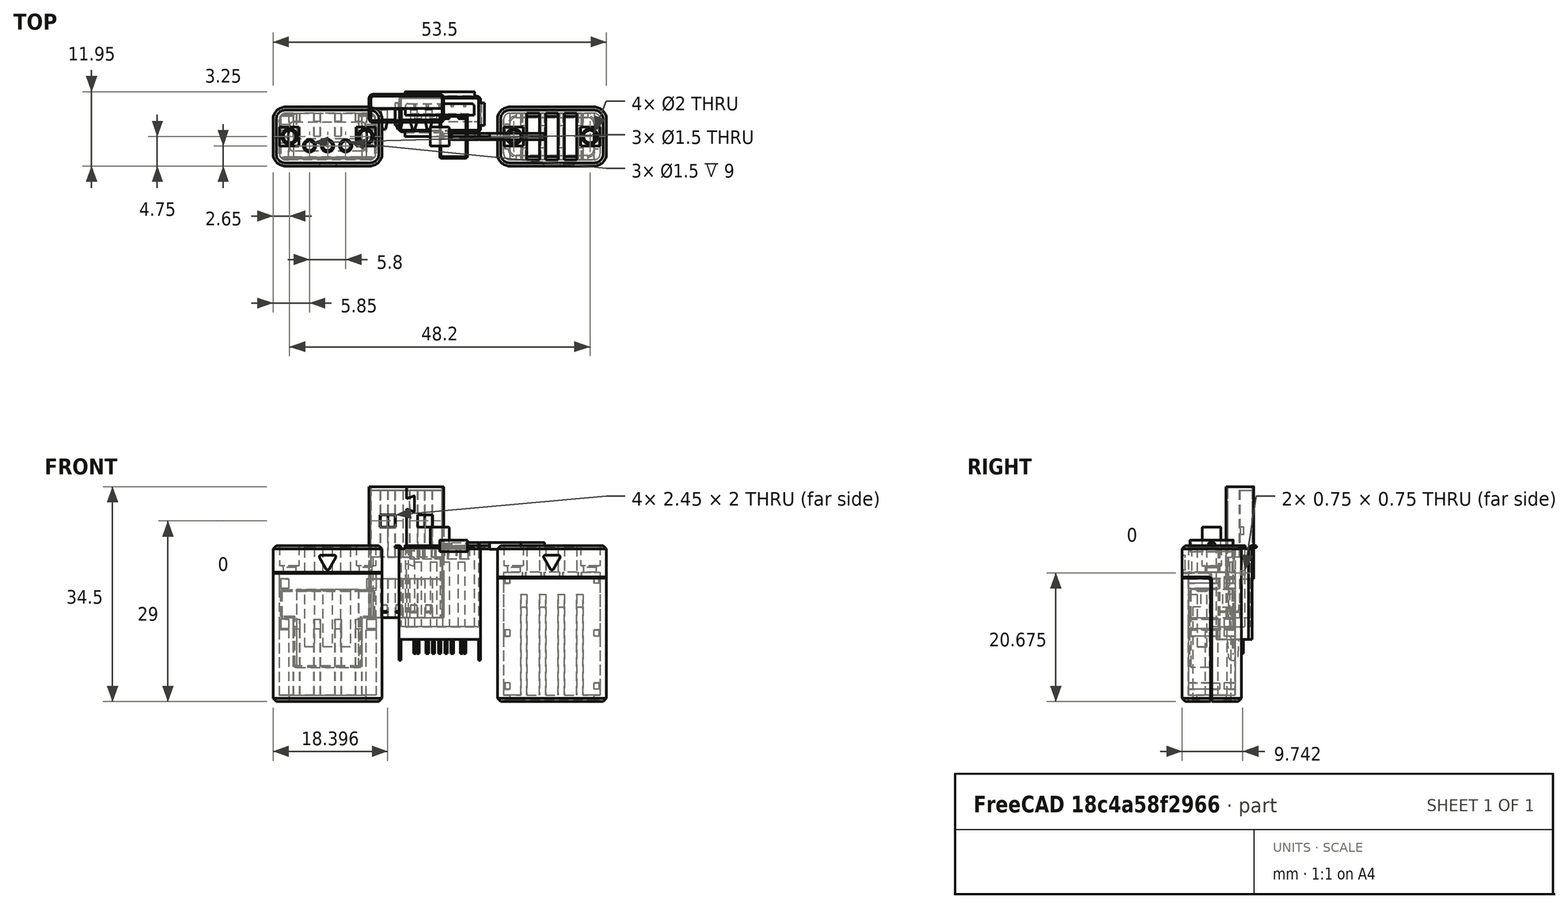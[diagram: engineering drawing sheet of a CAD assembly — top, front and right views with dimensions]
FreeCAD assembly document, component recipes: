
FREECAD ASSEMBLY — COMPONENT RECIPES ("test_v0.1_with_parts_I_have")

This assembly document has 13 components, labeled P0..P12 below (a component is one placed body or linked part). 10 of them carry a construction recipe — the FreeCAD feature program that regenerates the part from scratch, quoted from this document or its linked companion documents; the rest are supplied as boundary geometry only. No exploded tour is included for this assembly.
COMPONENT P0 — recipe-attached ("Housing-USB_Female", modeled in this document).
Construction recipe (the document's own serialized feature program — sketch geometry with constraints, then the solid features built on it; lengths are millimeters unless a unit is written):

FEATURE [PartDesign::FeatureBase] Clone
  BaseFeature = -> Chamfer002
FEATURE [Sketcher::SketchObject] Sketch020
  FullyConstrained = true
  MapMode = 5
  Support = -> [XY_Plane009]
  sketch-geometry (16):
    g0: LineSegment StartX=-1 StartY=3.75 StartZ=0 EndX=1 EndY=3.75 EndZ=0
    g1: LineSegment StartX=1 StartY=3.75 StartZ=0 EndX=1 EndY=3.25 EndZ=0
    g2: LineSegment StartX=1 StartY=3.25 StartZ=0 EndX=-1 EndY=3.25 EndZ=0
    g3: LineSegment StartX=-1 StartY=3.25 StartZ=0 EndX=-1 EndY=3.75 EndZ=0
    g4: LineSegment StartX=2 StartY=3.75 StartZ=0 EndX=4 EndY=3.75 EndZ=0
    g5: LineSegment StartX=4 StartY=3.75 StartZ=0 EndX=4 EndY=3.25 EndZ=0
    g6: LineSegment StartX=4 StartY=3.25 StartZ=0 EndX=2 EndY=3.25 EndZ=0
    g7: LineSegment StartX=2 StartY=3.25 StartZ=0 EndX=2 EndY=3.75 EndZ=0
    g8: LineSegment StartX=-4 StartY=3.75 StartZ=0 EndX=-2 EndY=3.75 EndZ=0
    g9: LineSegment StartX=-2 StartY=3.75 StartZ=0 EndX=-2 EndY=3.25 EndZ=0
    g10: LineSegment StartX=-2 StartY=3.25 StartZ=0 EndX=-4 EndY=3.25 EndZ=0
    g11: LineSegment StartX=-4 StartY=3.25 StartZ=0 EndX=-4 EndY=3.75 EndZ=0
    g12: LineSegment StartX=-2 StartY=3.75 StartZ=0 EndX=-1 EndY=3.75 EndZ=0
    g13: LineSegment StartX=1 StartY=3.75 StartZ=0 EndX=2 EndY=3.75 EndZ=0
    g14: LineSegment StartX=0 StartY=3.75 StartZ=0 EndX=0 EndY=3.5 EndZ=0
    g15: LineSegment StartX=0 StartY=3.5 StartZ=0 EndX=0 EndY=3.25 EndZ=0
  constraints (46):
    c: Coincident(g0,g1)
    c: Coincident(g1,g2)
    c: Coincident(g2,g3)
    c: Coincident(g3,g0)
    c: Horizontal(g2)
    c: Vertical(g1)
    c: Vertical(g3)
    c: Coincident(g4,g5)
    c: Coincident(g5,g6)
    c: Coincident(g6,g7)
    c: Coincident(g7,g4)
    c: Horizontal(g4)
    c: Horizontal(g6)
    c: Vertical(g5)
    c: Vertical(g7)
    c: Coincident(g8,g9)
    c: Coincident(g9,g10)
    c: Coincident(g10,g11)
    c: Coincident(g11,g8)
    c: Horizontal(g8)
    c: Horizontal(g10)
    c: Vertical(g9)
    c: Vertical(g11)
    c: Equal(g0,g8)
    c: Equal(g8,g4)
    c: Equal(g3,g7)
    c: Equal(g7,g11)
    c: Coincident(g12,g8)
    c: Coincident(g12,g0)
    c: Horizontal(g12)
    c: Coincident(g13,g0)
    c: Coincident(g13,g4)
    c: Horizontal(g13)
    c: PointOnObject(g14,g0)
    c: PointOnObject(g14,g-2)
    c: Coincident(g15,g14)
    c: PointOnObject(g15,g2)
    c: Vertical(g15)
    c: Vertical(g14)
    c: Equal(g15,g14)
    c: DistanceY(g14) = 3.5
    c: DistanceY(g5,g5) = 0.5
    c: Symmetric(g0,g0,g-2)
    c: Equal(g12,g13)
    c: DistanceX(g2,g2) = 2
    c: DistanceX(g13,g13) = 1
FEATURE [PartDesign::Pocket] Pocket013  label="contacts_slots"
  BaseFeature = -> Clone
  Direction = (0,0,-1)
  Length = 5
  Length2 = 5
  Profile = -> Sketch020
  ReferenceAxis = -> Sketch020 [N_Axis]
  Type = 1
FEATURE [PartDesign::Mirrored] Mirrored
  BaseFeature = -> Pocket013
  MirrorPlane = -> Sketch020 [H_Axis]
  Originals = -> [Pocket013]
FEATURE [PartDesign::CoordinateSystem] LCS_1
  AttacherType = Attacher::AttachEngine3D
  MapMode = 45
  Placement = pos=(-6.578e-13,1e-16,0) rot=(0,0,1;1.5708rad)
  Support = -> [Mirrored]
FEATURE [Sketcher::SketchObject] Sketch022
  FullyConstrained = true
  MapMode = 5
  Support = -> [XY_Plane009]
  expr: Constraints[9] = (9.2 + 3) / 2
  sketch-geometry (5):
    g0: Circle CenterX=0 CenterY=0 CenterZ=0 NormalX=0 NormalY=0 NormalZ=1 AngleXU=0 Radius=0.75
    g1: Circle CenterX=2.9 CenterY=0 CenterZ=0 NormalX=0 NormalY=0 NormalZ=1 AngleXU=0 Radius=0.75
    g2: Circle CenterX=-2.9 CenterY=0 CenterZ=0 NormalX=0 NormalY=0 NormalZ=1 AngleXU=0 Radius=0.75
    g3: Circle CenterX=-6.1 CenterY=0 CenterZ=0 NormalX=0 NormalY=0 NormalZ=1 AngleXU=0 Radius=1
    g4: Circle CenterX=6.1 CenterY=0 CenterZ=0 NormalX=0 NormalY=0 NormalZ=1 AngleXU=0 Radius=1
  constraints (12):
    c: Coincident(g0,g-1)
    c: PointOnObject(g1,g-1)
    c: Equal(g1,g0)
    c: Equal(g0,g2)
    c: PointOnObject(g3,g-1)
    c: Equal(g4,g3)
    c: Symmetric(g4,g3,g-2)
    c: Symmetric(g1,g2,g-2)
    c: DistanceX(g1) = 2.9
    c: DistanceX(g4) = 6.1
    c: Diameter(g0) = 1.5
    c: Diameter(g4) = 2
FEATURE [PartDesign::Pocket] Pocket014  label="pins001"
  BaseFeature = -> Mirrored
  Direction = (0,0,-1)
  Length = 5
  Length2 = 5
  Midplane = true
  Profile = -> Sketch022
  ReferenceAxis = -> Sketch022 [N_Axis]
  Type = 1
FEATURE [PartDesign::Chamfer] Chamfer004
  Angle = 45
  Base = -> Pocket014 [Edge181,Edge211,Edge212]
  BaseFeature = -> Pocket014
  ChamferType = 0
  FlipDirection = false
  Size = 0.25
  Size2 = 1
  SupportTransform = false
  UseAllEdges = false
FEATURE [Sketcher::SketchObject] Sketch023
  AttachmentOffset = pos=(0,0,-4.2) rot=(0,0,1;0rad)
  FullyConstrained = false
  MapMode = 5
  Placement = pos=(0,0,-4.2) rot=(0,0,1;0rad)
  Support = -> [XY_Plane009]
  expr: Constraints[63] = 2 + 1
  sketch-geometry (23):
    g0: LineSegment StartX=-1.75 StartY=4 StartZ=0 EndX=-1.25 EndY=4 EndZ=0
    g1: LineSegment StartX=-1.25 StartY=4 StartZ=0 EndX=-1.25 EndY=-4 EndZ=0
    g2: LineSegment StartX=-1.25 StartY=-4 StartZ=0 EndX=-1.75 EndY=-4 EndZ=0
    g3: LineSegment StartX=-1.75 StartY=-4 StartZ=0 EndX=-1.75 EndY=4 EndZ=0
    g4: LineSegment StartX=1.25 StartY=4 StartZ=0 EndX=1.75 EndY=4 EndZ=0
    g5: LineSegment StartX=1.75 StartY=4 StartZ=0 EndX=1.75 EndY=-4 EndZ=0
    g6: LineSegment StartX=1.75 StartY=-4 StartZ=0 EndX=1.25 EndY=-4 EndZ=0
    g7: LineSegment StartX=1.25 StartY=-4 StartZ=0 EndX=1.25 EndY=4 EndZ=0
    g8: LineSegment StartX=-4.25 StartY=4 StartZ=0 EndX=-4.75 EndY=4 EndZ=0
    g9: LineSegment StartX=-4.75 StartY=4 StartZ=0 EndX=-4.75 EndY=-4 EndZ=0
    g10: LineSegment StartX=-4.75 StartY=-4 StartZ=0 EndX=-4.25 EndY=-4 EndZ=0
    g11: LineSegment StartX=-4.25 StartY=-4 StartZ=0 EndX=-4.25 EndY=4 EndZ=0
    g12: LineSegment StartX=4.75 StartY=4 StartZ=0 EndX=4.25 EndY=4 EndZ=0
    g13: LineSegment StartX=4.25 StartY=4 StartZ=0 EndX=4.25 EndY=-4 EndZ=0
    g14: LineSegment StartX=4.25 StartY=-4 StartZ=0 EndX=4.75 EndY=-4 EndZ=0
    g15: LineSegment StartX=4.75 StartY=-4 StartZ=0 EndX=4.75 EndY=4 EndZ=0
    g16: LineSegment StartX=4.25 StartY=4 StartZ=0 EndX=1.75 EndY=4 EndZ=0
    g17: LineSegment StartX=1.25 StartY=4 StartZ=0 EndX=-1.25 EndY=4 EndZ=0
    g18: LineSegment StartX=-1.75 StartY=4 StartZ=0 EndX=-4.25 EndY=4 EndZ=0
    g19: LineSegment StartX=1.25 StartY=3.42637 StartZ=0 EndX=1.5 EndY=3.42637 EndZ=0
    g20: LineSegment StartX=1.5 StartY=3.42637 StartZ=0 EndX=1.75 EndY=3.42637 EndZ=0
    g21: LineSegment StartX=-1.75 StartY=3.36901 StartZ=0 EndX=-1.5 EndY=3.36901 EndZ=0
    g22: LineSegment StartX=-1.5 StartY=3.36901 StartZ=0 EndX=-1.25 EndY=3.36901 EndZ=0
  constraints (64):
    c: Coincident(g0,g1)
    c: Coincident(g1,g2)
    c: Coincident(g2,g3)
    c: Coincident(g3,g0)
    c: Horizontal(g0)
    c: Horizontal(g2)
    c: Vertical(g1)
    c: Vertical(g3)
    c: Coincident(g4,g5)
    c: Coincident(g5,g6)
    c: Coincident(g6,g7)
    c: Coincident(g7,g4)
    c: Horizontal(g4)
    c: Horizontal(g6)
    c: Vertical(g5)
    c: Vertical(g7)
    c: Coincident(g8,g9)
    c: Coincident(g9,g10)
    c: Coincident(g10,g11)
    c: Coincident(g11,g8)
    c: Horizontal(g8)
    c: Horizontal(g10)
    c: Vertical(g9)
    c: Vertical(g11)
    c: Coincident(g12,g13)
    c: Coincident(g13,g14)
    c: Coincident(g14,g15)
    c: Coincident(g15,g12)
    c: Horizontal(g12)
    c: Horizontal(g14)
    c: Vertical(g13)
    c: Equal(g12,g4)
    c: Equal(g4,g0)
    c: Equal(g0,g8)
    c: Coincident(g16,g12)
    c: Coincident(g16,g4)
    c: Horizontal(g16)
    c: Coincident(g17,g4)
    c: Coincident(g17,g0)
    c: Coincident(g18,g0)
    c: Coincident(g18,g8)
    c: Horizontal(g18)
    c: Symmetric(g14,g12,g-1)
    c: Horizontal(g13,g5)
    c: Horizontal(g5,g1)
    c: Horizontal(g1,g10)
    c: DistanceY(g15,g15) = 8
    c: DistanceX(g4,g4) = 0.5
    c: Symmetric(g4,g0,g-2)
    c: Equal(g16,g17)
    c: Equal(g17,g18)
    c: PointOnObject(g19,g7)
    c: Coincident(g20,g19)
    c: PointOnObject(g20,g5)
    c: Horizontal(g20)
    c: PointOnObject(g21,g3)
    c: Horizontal(g21)
    c: Coincident(g22,g21)
    c: PointOnObject(g22,g1)
    c: Horizontal(g22)
    c: Equal(g22,g21)
    c: Equal(g20,g19)
    c: Horizontal(g19)
    c: DistanceX(g21,g19) = 3
FEATURE [PartDesign::Pad] Pad007  label="spacers"
  BaseFeature = -> Chamfer004
  Direction = (0,0,1)
  Length = 1
  Length2 = 10
  Profile = -> Sketch023
  ReferenceAxis = -> Sketch023 [N_Axis]
  Reversed = true
  Type = 0
FEATURE [Sketcher::SketchObject] Sketch024
  FullyConstrained = true
  MapMode = 5
  Support = -> [XY_Plane009]
  sketch-geometry (16):
    g0: LineSegment StartX=-1 StartY=3.75 StartZ=0 EndX=1 EndY=3.75 EndZ=0
    g1: LineSegment StartX=1 StartY=3.75 StartZ=0 EndX=1 EndY=-3.75 EndZ=0
    g2: LineSegment StartX=1 StartY=-3.75 StartZ=0 EndX=-1 EndY=-3.75 EndZ=0
    g3: LineSegment StartX=-1 StartY=-3.75 StartZ=0 EndX=-1 EndY=3.75 EndZ=0
    g4: LineSegment StartX=2 StartY=3.75 StartZ=0 EndX=4 EndY=3.75 EndZ=0
    g5: LineSegment StartX=4 StartY=3.75 StartZ=0 EndX=4 EndY=-3.75 EndZ=0
    g6: LineSegment StartX=4 StartY=-3.75 StartZ=0 EndX=2 EndY=-3.75 EndZ=0
    g7: LineSegment StartX=2 StartY=-3.75 StartZ=0 EndX=2 EndY=3.75 EndZ=0
    g8: LineSegment StartX=-4 StartY=3.75 StartZ=0 EndX=-2 EndY=3.75 EndZ=0
    g9: LineSegment StartX=-2 StartY=3.75 StartZ=0 EndX=-2 EndY=-3.75 EndZ=0
    g10: LineSegment StartX=-2 StartY=-3.75 StartZ=0 EndX=-4 EndY=-3.75 EndZ=0
    g11: LineSegment StartX=-4 StartY=-3.75 StartZ=0 EndX=-4 EndY=3.75 EndZ=0
    g12: LineSegment StartX=-2 StartY=3.75 StartZ=0 EndX=-1 EndY=3.75 EndZ=0
    g13: LineSegment StartX=1 StartY=3.75 StartZ=0 EndX=2 EndY=3.75 EndZ=0
    g14: LineSegment StartX=0 StartY=3.75 StartZ=0 EndX=0 EndY=0 EndZ=0
    g15: LineSegment StartX=0 StartY=0 StartZ=0 EndX=0 EndY=-3.75 EndZ=0
  constraints (45):
    c: Coincident(g0,g1)
    c: Coincident(g1,g2)
    c: Coincident(g2,g3)
    c: Coincident(g3,g0)
    c: Horizontal(g2)
    c: Vertical(g1)
    c: Vertical(g3)
    c: Coincident(g4,g5)
    c: Coincident(g5,g6)
    c: Coincident(g6,g7)
    c: Coincident(g7,g4)
    c: Horizontal(g4)
    c: Horizontal(g6)
    c: Vertical(g5)
    c: Vertical(g7)
    c: Coincident(g8,g9)
    c: Coincident(g9,g10)
    c: Coincident(g10,g11)
    c: Coincident(g11,g8)
    c: Horizontal(g8)
    c: Horizontal(g10)
    c: Vertical(g9)
    c: Vertical(g11)
    c: Equal(g0,g8)
    c: Equal(g8,g4)
    c: Equal(g3,g7)
    c: Equal(g7,g11)
    c: Coincident(g12,g8)
    c: Coincident(g12,g0)
    c: Horizontal(g12)
    c: Coincident(g13,g0)
    c: Coincident(g13,g4)
    c: Horizontal(g13)
    c: PointOnObject(g14,g0)
    c: Coincident(g15,g14)
    c: PointOnObject(g15,g2)
    c: Vertical(g15)
    c: Vertical(g14)
    c: Equal(g15,g14)
    c: DistanceY(g5,g5) = 7.5
    c: Symmetric(g0,g0,g-2)
    c: Equal(g12,g13)
    c: DistanceX(g2,g2) = 2
    c: DistanceX(g13,g13) = 1
    c: Coincident(g14,g-1)
FEATURE [PartDesign::Pocket] Pocket015  label="contacts_space"
  BaseFeature = -> Pad007
  Direction = (0,0,-1)
  Length = 0.2
  Length2 = 5
  Profile = -> Sketch024
  ReferenceAxis = -> Sketch024 [N_Axis]
  Refine = true
  Type = 0
FEATURE [Sketcher::SketchObject] Sketch025
  AttachmentOffset = pos=(0,0,-24) rot=(0,0,1;0rad)
  FullyConstrained = true
  MapMode = 5
  Placement = pos=(0,0,-24) rot=(0,0,1;0rad)
  Support = -> [XY_Plane008]
  sketch-geometry (8):
    g0: LineSegment StartX=-6.75 StartY=4.75 StartZ=0 EndX=6.75 EndY=4.75 EndZ=0
    g1: LineSegment StartX=8.75 StartY=2.75 StartZ=0 EndX=8.75 EndY=-2.75 EndZ=0
    g2: LineSegment StartX=6.75 StartY=-4.75 StartZ=0 EndX=-6.75 EndY=-4.75 EndZ=0
    g3: LineSegment StartX=-8.75 StartY=-2.75 StartZ=0 EndX=-8.75 EndY=2.75 EndZ=0
    g4: ArcOfCircle CenterX=6.75 CenterY=2.75 CenterZ=0 NormalX=0 NormalY=0 NormalZ=1 AngleXU=0 Radius=2 StartAngle=0 EndAngle=1.5708
    g5: ArcOfCircle CenterX=6.75 CenterY=-2.75 CenterZ=0 NormalX=0 NormalY=0 NormalZ=1 AngleXU=0 Radius=2 StartAngle=4.71239 EndAngle=6.28319
    g6: ArcOfCircle CenterX=-6.75 CenterY=-2.75 CenterZ=0 NormalX=0 NormalY=0 NormalZ=1 AngleXU=0 Radius=2 StartAngle=3.14159 EndAngle=4.71239
    g7: ArcOfCircle CenterX=-6.75 CenterY=2.75 CenterZ=0 NormalX=0 NormalY=0 NormalZ=1 AngleXU=0 Radius=2 StartAngle=1.5708 EndAngle=3.14159
  constraints (19):
    c: Horizontal(g0)
    c: Horizontal(g2)
    c: Vertical(g1)
    c: Vertical(g3)
    c: Tangent(g0,g4) = 1.5708
    c: Tangent(g1,g4) = 1.5708
    c: Tangent(g1,g5) = 1.5708
    c: Tangent(g2,g5) = 1.5708
    c: Tangent(g2,g6) = 1.5708
    c: Tangent(g3,g6) = 1.5708
    c: Tangent(g0,g7) = 1.5708
    c: Tangent(g3,g7) = 1.5708
    c: Equal(g7,g6)
    c: Equal(g6,g5)
    c: Equal(g5,g4)
    c: Symmetric(g7,g5,g-1)
    c: DistanceY(g2,g0) = 9.5
    c: DistanceX(g3,g1) = 17.5
    c: Radius(g4) = 2
FEATURE [PartDesign::Pad] Pad008  label="back_wall"
  BaseFeature = -> Pocket015
  Direction = (0,0,1)
  Length = 1
  Length2 = 10
  Profile = -> Sketch025
  ReferenceAxis = -> Sketch025 [N_Axis]
  Refine = true
  Reversed = true
  Type = 0
FEATURE [Sketcher::SketchObject] Sketch030
  AttachmentOffset = pos=(0,0,-24) rot=(0,0,1;0rad)
  FullyConstrained = true
  MapMode = 5
  Placement = pos=(0,0,-24) rot=(0,0,1;0rad)
  Support = -> [XY_Plane009]
  expr: Constraints[20] = 13.1 + 0.4
  expr: Constraints[22] = 5.7 + 0.4
  sketch-geometry (10):
    g0: ArcOfCircle CenterX=-5.75 CenterY=2.05 CenterZ=0 NormalX=0 NormalY=0 NormalZ=1 AngleXU=0 Radius=1 StartAngle=1.5708 EndAngle=3.14159
    g1: LineSegment StartX=-5.75 StartY=3.05 StartZ=0 EndX=5.75 EndY=3.05 EndZ=0
    g2: ArcOfCircle CenterX=5.75 CenterY=2.05 CenterZ=0 NormalX=0 NormalY=0 NormalZ=1 AngleXU=0 Radius=1 StartAngle=5e-16 EndAngle=1.5708
    g3: LineSegment StartX=6.75 StartY=2.05 StartZ=0 EndX=6.75 EndY=-2.05 EndZ=0
    g4: ArcOfCircle CenterX=5.75 CenterY=-2.05 CenterZ=0 NormalX=0 NormalY=0 NormalZ=1 AngleXU=0 Radius=1 StartAngle=4.71239 EndAngle=6.28319
    g5: LineSegment StartX=5.75 StartY=-3.05 StartZ=0 EndX=-5.75 EndY=-3.05 EndZ=0
    g6: ArcOfCircle CenterX=-5.75 CenterY=-2.05 CenterZ=0 NormalX=0 NormalY=0 NormalZ=1 AngleXU=0 Radius=1 StartAngle=3.14159 EndAngle=4.71239
    g7: LineSegment StartX=-6.75 StartY=-2.05 StartZ=0 EndX=-6.75 EndY=2.05 EndZ=0
    g8: GeomPoint X=-6.75 Y=3.05 Z=0
    g9: GeomPoint X=6.75 Y=-3.05 Z=0
  constraints (23):
    c: Tangent(g0,g1) = 1.5708
    c: Tangent(g1,g2) = 1.5708
    c: Tangent(g2,g3) = 1.5708
    c: Tangent(g3,g4) = 1.5708
    c: Tangent(g4,g5) = 1.5708
    c: Tangent(g5,g6) = 1.5708
    c: Tangent(g6,g7) = 1.5708
    c: Tangent(g7,g0) = 1.5708
    c: Horizontal(g1)
    c: Horizontal(g5)
    c: Vertical(g3)
    c: Vertical(g7)
    c: Equal(g0,g2)
    c: Equal(g2,g4)
    c: Equal(g4,g6)
    c: PointOnObject(g8,g1)
    c: PointOnObject(g8,g7)
    c: PointOnObject(g9,g3)
    c: PointOnObject(g9,g5)
    c: Symmetric(g9,g8,g-1)
    c: DistanceX(g0,g2) = 13.5
    c: Radius(g2) = 1
    c: DistanceY(g4,g1) = 6.1
FEATURE [PartDesign::Pocket] Pocket017
  BaseFeature = -> Pad008
  Direction = (0,0,-1)
  Length = 5
  Length2 = 5
  Profile = -> Sketch030
  ReferenceAxis = -> Sketch030 [N_Axis]
  Refine = true
  Type = 1
FEATURE [PartDesign::Chamfer] Chamfer005
  Angle = 45
  Base = -> Pocket017 [Edge8]
  BaseFeature = -> Pocket017
  ChamferType = 0
  FlipDirection = false
  Size = 0.5
  Size2 = 1
  SupportTransform = false
  UseAllEdges = false
FEATURE [PartDesign::Chamfer] Chamfer006
  Angle = 45
  Base = -> Chamfer005 [Edge16]
  BaseFeature = -> Chamfer005
  ChamferType = 0
  FlipDirection = false
  Size = 0.25
  Size2 = 1
  SupportTransform = false
  UseAllEdges = false
FEATURE [Sketcher::SketchObject] Sketch031
  AttachmentOffset = pos=(0,0,-25) rot=(0,0,1;0rad)
  FullyConstrained = true
  MapMode = 5
  Placement = pos=(0,0,-25) rot=(0,0,1;0rad)
  Support = -> [XY_Plane009]
  expr: Constraints[20] = 12.5 + 0.4 + 2
  expr: Constraints[21] = 5.1 + 0.4 + 2
  sketch-geometry (18):
    g0: ArcOfCircle CenterX=-5.75 CenterY=2.05 CenterZ=0 NormalX=0 NormalY=0 NormalZ=1 AngleXU=0 Radius=1.7 StartAngle=1.5708 EndAngle=3.14159
    g1: LineSegment StartX=-5.75 StartY=3.75 StartZ=0 EndX=5.75 EndY=3.75 EndZ=0
    g2: ArcOfCircle CenterX=5.75 CenterY=2.05 CenterZ=0 NormalX=0 NormalY=0 NormalZ=1 AngleXU=0 Radius=1.7 StartAngle=4.6506e-12 EndAngle=1.5708
    g3: LineSegment StartX=7.45 StartY=2.05 StartZ=0 EndX=7.45 EndY=-2.05 EndZ=0
    g4: ArcOfCircle CenterX=5.75 CenterY=-2.05 CenterZ=0 NormalX=0 NormalY=0 NormalZ=1 AngleXU=0 Radius=1.7 StartAngle=4.71239 EndAngle=6.28319
    g5: LineSegment StartX=5.75 StartY=-3.75 StartZ=0 EndX=-5.75 EndY=-3.75 EndZ=0
    g6: ArcOfCircle CenterX=-5.75 CenterY=-2.05 CenterZ=0 NormalX=0 NormalY=0 NormalZ=1 AngleXU=0 Radius=1.7 StartAngle=3.14159 EndAngle=4.71239
    g7: LineSegment StartX=-7.45 StartY=-2.05 StartZ=0 EndX=-7.45 EndY=2.05 EndZ=0
    g8: GeomPoint X=-7.45 Y=3.75 Z=0
    g9: GeomPoint X=7.45 Y=-3.75 Z=0
    g10: LineSegment StartX=-5.75 StartY=3.75 StartZ=0 EndX=-5.75 EndY=2.05 EndZ=0
    g11: LineSegment StartX=5.75 StartY=3.75 StartZ=0 EndX=5.75 EndY=2.05 EndZ=0
    g12: LineSegment StartX=7.45 StartY=-2.05 StartZ=0 EndX=5.75 EndY=-2.05 EndZ=0
    g13: LineSegment StartX=-7.45 StartY=2.05 StartZ=0 EndX=-5.75 EndY=2.05 EndZ=0
    g14: LineSegment StartX=5.75 StartY=2.05 StartZ=0 EndX=7.45 EndY=2.05 EndZ=0
    g15: LineSegment StartX=5.75 StartY=-2.05 StartZ=0 EndX=5.75 EndY=-3.75 EndZ=0
    g16: LineSegment StartX=-5.75 StartY=-2.05 StartZ=0 EndX=-7.45 EndY=-2.05 EndZ=0
    g17: LineSegment StartX=-5.75 StartY=-2.05 StartZ=0 EndX=-5.75 EndY=-3.75 EndZ=0
  constraints (39):
    c: Tangent(g0,g1) = 1.5708
    c: Tangent(g1,g2) = 1.5708
    c: Tangent(g2,g3) = 1.5708
    c: Tangent(g3,g4) = 1.5708
    c: Tangent(g4,g5) = 1.5708
    c: Tangent(g5,g6) = 1.5708
    c: Tangent(g6,g7) = 1.5708
    c: Tangent(g7,g0) = 1.5708
    c: Horizontal(g1)
    c: Horizontal(g5)
    c: Vertical(g3)
    c: Vertical(g7)
    c: Equal(g0,g2)
    c: Equal(g2,g4)
    c: Equal(g4,g6)
    c: PointOnObject(g8,g1)
    c: PointOnObject(g8,g7)
    c: PointOnObject(g9,g3)
    c: PointOnObject(g9,g5)
    c: Symmetric(g9,g8,g-1)
    c: DistanceX(g0,g2) = 14.9
    c: DistanceY(g4,g1) = 7.5
    c: Coincident(g10,g0)
    c: Coincident(g17,g5)
    c: Coincident(g11,g1)
    c: Coincident(g15,g4)
    c: Coincident(g12,g3)
    c: Coincident(g16,g6)
    c: Coincident(g13,g0)
    c: Coincident(g14,g2)
    c: Coincident(g11,g14)
    c: Coincident(g12,g15)
    c: Coincident(g10,g13)
    c: Coincident(g17,g16)
    c: Coincident(g0,g10)
    c: Coincident(g2,g11)
    c: Coincident(g4,g12)
    c: Coincident(g6,g16)
    c: DistanceX(g1,g1) = 11.5
FEATURE [PartDesign::Pocket] Pocket018  label="usb_dent"
  BaseFeature = -> Chamfer006
  Direction = (0,0,-1)
  Length = 0.4
  Length2 = 5
  Profile = -> Sketch031
  ReferenceAxis = -> Sketch031 [N_Axis]
  Refine = true
  Reversed = true
  Type = 0
FEATURE [Sketcher::SketchObject] Sketch034
  AttachmentOffset = pos=(0,0,4.5) rot=(0,0,1;0rad)
  FullyConstrained = true
  MapMode = 5
  Placement = pos=(4.5,-1e-15,1e-15) rot=(0.57735,0.57735,0.57735;2.0944rad)
  Support = -> [YZ_Plane009]
  sketch-geometry (6):
    g0: LineSegment StartX=3.05 StartY=-24 StartZ=0 EndX=3.75 EndY=-24 EndZ=0
    g1: LineSegment StartX=3.75 StartY=-24 StartZ=0 EndX=3.75 EndY=-7.8 EndZ=0
    g2: LineSegment StartX=3.75 StartY=-7.8 StartZ=0 EndX=1.75 EndY=-7.8 EndZ=0
    g3: LineSegment StartX=1.75 StartY=-7.8 StartZ=0 EndX=1.75 EndY=-9.8 EndZ=0
    g4: LineSegment StartX=1.75 StartY=-9.8 StartZ=0 EndX=3.05 EndY=-9.8 EndZ=0
    g5: LineSegment StartX=3.05 StartY=-9.8 StartZ=0 EndX=3.05 EndY=-24 EndZ=0
  constraints (18):
    c: Horizontal(g0)
    c: Coincident(g0,g1)
    c: Vertical(g1)
    c: Coincident(g1,g2)
    c: Horizontal(g2)
    c: Coincident(g2,g3)
    c: Vertical(g3)
    c: Coincident(g3,g4)
    c: Horizontal(g4)
    c: Coincident(g4,g5)
    c: Coincident(g5,g0)
    c: Vertical(g5)
    c: DistanceY(g0) = -24
    c: DistanceX(g0) = 3.75
    c: DistanceX(g0,g0) = 0.7
    c: DistanceX(g2,g2) = 2
    c: DistanceY(g3,g3) = 2
    c: DistanceY(g5,g5) = 14.2
FEATURE [PartDesign::Pad] Pad011
  BaseFeature = -> Pocket018
  Direction = (1,-2e-16,3e-16)
  Length = 1
  Length2 = 10
  Midplane = true
  Profile = -> Sketch034
  ReferenceAxis = -> Sketch034 [N_Axis]
  Type = 0
FEATURE [PartDesign::LinearPattern] LinearPattern
  Direction = -> Sketch034 [N_Axis]
  Length = 9
  Occurrences = 4
  Reversed = true
FEATURE [PartDesign::Mirrored] Mirrored002
  MirrorPlane = -> Sketch034 [V_Axis]
FEATURE [PartDesign::MultiTransform] MultiTransform
  BaseFeature = -> Pad011
  Originals = -> [Pad011]
  Transformations = -> [LinearPattern,Mirrored002]
FEATURE [Sketcher::SketchObject] Sketch036
  FullyConstrained = true
  MapMode = 5
  Placement = pos=(0,0,0) rot=(1,0,0;1.5708rad)
  Support = -> [XZ_Plane009]
  sketch-geometry (17):
    g0: LineSegment StartX=6.75 StartY=-5 StartZ=0 EndX=7.75 EndY=-5 EndZ=0
    g1: LineSegment StartX=7.75 StartY=-5 StartZ=0 EndX=7.75 EndY=-6 EndZ=0
    g2: LineSegment StartX=7.75 StartY=-6 StartZ=0 EndX=6.75 EndY=-6 EndZ=0
    g3: LineSegment StartX=6.75 StartY=-6 StartZ=0 EndX=6.75 EndY=-5 EndZ=0
    g4: LineSegment StartX=7.75 StartY=-23 StartZ=0 EndX=6.75 EndY=-23 EndZ=0
    g5: LineSegment StartX=6.75 StartY=-23 StartZ=0 EndX=6.75 EndY=-22 EndZ=0
    g6: LineSegment StartX=6.75 StartY=-22 StartZ=0 EndX=7.75 EndY=-22 EndZ=0
    g7: LineSegment StartX=7.75 StartY=-22 StartZ=0 EndX=7.75 EndY=-23 EndZ=0
    g8: LineSegment StartX=7.75 StartY=-14.5 StartZ=0 EndX=6.75 EndY=-14.5 EndZ=0
    g9: LineSegment StartX=6.75 StartY=-14.5 StartZ=0 EndX=6.75 EndY=-13.5 EndZ=0
    g10: LineSegment StartX=6.75 StartY=-13.5 StartZ=0 EndX=7.75 EndY=-13.5 EndZ=0
    g11: LineSegment StartX=7.75 StartY=-13.5 StartZ=0 EndX=7.75 EndY=-14.5 EndZ=0
    g12: LineSegment StartX=7.75 StartY=-6 StartZ=0 EndX=7.75 EndY=-13.5 EndZ=0
    g13: LineSegment StartX=7.75 StartY=-14.5 StartZ=0 EndX=7.75 EndY=-22 EndZ=0
    g14: LineSegment StartX=6.75 StartY=-13.5 StartZ=0 EndX=7.75 EndY=-14.5 EndZ=0
    g15: LineSegment StartX=7.75 StartY=-13.5 StartZ=0 EndX=6.75 EndY=-14.5 EndZ=0
    g16: GeomPoint X=7.25 Y=-14 Z=0
  constraints (46):
    c: Coincident(g0,g1)
    c: Coincident(g1,g2)
    c: Coincident(g2,g3)
    c: Coincident(g3,g0)
    c: Horizontal(g0)
    c: Horizontal(g2)
    c: Vertical(g1)
    c: Vertical(g3)
    c: Coincident(g4,g5)
    c: Coincident(g5,g6)
    c: Coincident(g6,g7)
    c: Coincident(g7,g4)
    c: Horizontal(g4)
    c: Horizontal(g6)
    c: Vertical(g5)
    c: Vertical(g7)
    c: Coincident(g8,g9)
    c: Coincident(g9,g10)
    c: Coincident(g10,g11)
    c: Coincident(g11,g8)
    c: Horizontal(g8)
    c: Horizontal(g10)
    c: Vertical(g9)
    c: Vertical(g11)
    c: Equal(g1,g11)
    c: Equal(g11,g7)
    c: Equal(g6,g10)
    c: Equal(g10,g0)
    c: Coincident(g12,g1)
    c: Coincident(g12,g10)
    c: Vertical(g12)
    c: Coincident(g13,g8)
    c: Coincident(g13,g6)
    c: Vertical(g13)
    c: Equal(g13,g12)
    c: Coincident(g14,g8)
    c: Coincident(g15,g10)
    c: Coincident(g15,g8)
    c: PointOnObject(g16,g14)
    c: PointOnObject(g16,g15)
    c: Coincident(g9,g14)
    c: DistanceY(g16) = -14
    c: DistanceY(g1,g1) = 1
    c: DistanceX(g0,g0) = 1
    c: DistanceY(g12,g12) = 7.5
    c: DistanceX(g-1,g4) = 7.75
FEATURE [PartDesign::Pad] Pad013
  BaseFeature = -> MultiTransform
  Direction = (0,-1,-2e-16)
  Length = 8
  Length2 = 10
  Midplane = true
  Profile = -> Sketch036
  ReferenceAxis = -> Sketch036 [N_Axis]
  Type = 0
FEATURE [PartDesign::Mirrored] Mirrored003
  BaseFeature = -> Pad013
  MirrorPlane = -> Sketch036 [V_Axis]
  Originals = -> [Pad013]
FEATURE [PartDesign::CoordinateSystem] LCS_mag003
  AttacherType = Attacher::AttachEngine3D
  MapMode = 45
  Placement = pos=(-6.20221,2e-16,-3.2) rot=(0,0,1;0rad)
  Support = -> [Mirrored003]
FEATURE [PartDesign::CoordinateSystem] LCS_mag004
  AttacherType = Attacher::AttachEngine3D
  MapMode = 45
  Placement = pos=(6.20221,4e-16,-3.2) rot=(0,0,1;0rad)
  Support = -> [Mirrored003]
FEATURE [PartDesign::CoordinateSystem] LCS_usb_connector
  AttacherType = Attacher::AttachEngine3D
  MapMode = 45
  Placement = pos=(-4e-16,3e-16,-24.6) rot=(0,0,1;1.5708rad)
  Support = -> [Mirrored003]
FEATURE [PartDesign::CoordinateSystem] LCS_contact1
  AttacherType = Attacher::AttachEngine3D
  MapMode = 45
  Placement = pos=(-3,0,-0.2) rot=(0,0,1;0rad)
  Support = -> [Mirrored003]
FEATURE [PartDesign::CoordinateSystem] LCS_contact2
  AttacherType = Attacher::AttachEngine3D
  MapMode = 45
  Placement = pos=(1e-16,-1e-16,-0.2) rot=(0,0,1;0rad)
  Support = -> [Mirrored003]
FEATURE [PartDesign::CoordinateSystem] LCS_contact  label="LCS_contact3"
  AttacherType = Attacher::AttachEngine3D
  MapMode = 45
  Placement = pos=(3,-1e-16,-0.2) rot=(0,0,1;0rad)
  Support = -> [Mirrored003]
FEATURE [PartDesign::Body] Body  label="Housing-USB_Female"
  BaseFeature = -> Chamfer002
  Group = -> [Clone,Sketch020,Pocket013,Mirrored,LCS_1,Sketch022,Pocket014,Chamfer004,LCS_mag003,LCS_mag004,Sketch023,Pad007,Sketch024,Pocket015,Sketch025,Pad008,Sketch030,Pocket017,Chamfer005,Chamfer006,LCS_usb_connector,LCS_contact1,LCS_contact2,LCS_contact,Sketch031,Pocket018,Sketch034,Pad011,MultiTransform,LinearPattern,Mirrored002,Sketch036,Pad013,Mirrored003]
  Origin = -> Origin009
  Tip = -> Mirrored003
COMPONENT P1 — recipe-attached ("USB-Female_Bot", modeled in this document).
Construction recipe (the document's own serialized feature program — sketch geometry with constraints, then the solid features built on it; lengths are millimeters unless a unit is written):

FEATURE [Sketcher::SketchObject] Sketch032
  FullyConstrained = true
  MapMode = 5
  Placement = pos=(0,0,0) rot=(0.57735,0.57735,0.57735;2.0944rad)
  Support = -> [YZ_Plane034]
  sketch-geometry (4):
    g0: LineSegment StartX=0 StartY=-25 StartZ=0 EndX=-8 EndY=-25 EndZ=0
    g1: LineSegment StartX=-8 StartY=-25 StartZ=0 EndX=-8 EndY=-5 EndZ=0
    g2: LineSegment StartX=-8 StartY=-5 StartZ=0 EndX=0 EndY=-5 EndZ=0
    g3: LineSegment StartX=0 StartY=-5 StartZ=0 EndX=0 EndY=-25 EndZ=0
  constraints (12):
    c: Coincident(g0,g1)
    c: Coincident(g1,g2)
    c: Coincident(g2,g3)
    c: Coincident(g3,g0)
    c: Horizontal(g0)
    c: Horizontal(g2)
    c: Vertical(g1)
    c: Vertical(g3)
    c: PointOnObject(g0,g-2)
    c: DistanceY(g1,g-1) = 5
    c: DistanceY(g1,g1) = 20
    c: DistanceX(g0,g0) = 8
FEATURE [PartDesign::FeatureBase] Clone005
  BaseFeature = -> Body
FEATURE [PartDesign::Pocket] Pocket019
  BaseFeature = -> Clone005
  Direction = (-1,2e-16,-3e-16)
  Length = 5
  Length2 = 5
  Midplane = true
  Profile = -> Sketch032
  ReferenceAxis = -> Sketch032 [N_Axis]
  Type = 1
FEATURE [Sketcher::SketchObject] Sketch037
  FullyConstrained = true
  MapMode = 5
  Placement = pos=(0,0,0) rot=(1,0,0;1.5708rad)
  Support = -> [XZ_Plane034]
  sketch-geometry (17):
    g0: LineSegment StartX=6.75 StartY=-5 StartZ=0 EndX=7.75 EndY=-5 EndZ=0
    g1: LineSegment StartX=7.75 StartY=-5 StartZ=0 EndX=7.75 EndY=-6 EndZ=0
    g2: LineSegment StartX=7.75 StartY=-6 StartZ=0 EndX=6.75 EndY=-6 EndZ=0
    g3: LineSegment StartX=6.75 StartY=-6 StartZ=0 EndX=6.75 EndY=-5 EndZ=0
    g4: LineSegment StartX=7.75 StartY=-23 StartZ=0 EndX=6.75 EndY=-23 EndZ=0
    g5: LineSegment StartX=6.75 StartY=-23 StartZ=0 EndX=6.75 EndY=-22 EndZ=0
    g6: LineSegment StartX=6.75 StartY=-22 StartZ=0 EndX=7.75 EndY=-22 EndZ=0
    g7: LineSegment StartX=7.75 StartY=-22 StartZ=0 EndX=7.75 EndY=-23 EndZ=0
    g8: LineSegment StartX=7.75 StartY=-14.5 StartZ=0 EndX=6.75 EndY=-14.5 EndZ=0
    g9: LineSegment StartX=6.75 StartY=-14.5 StartZ=0 EndX=6.75 EndY=-13.5 EndZ=0
    g10: LineSegment StartX=6.75 StartY=-13.5 StartZ=0 EndX=7.75 EndY=-13.5 EndZ=0
    g11: LineSegment StartX=7.75 StartY=-13.5 StartZ=0 EndX=7.75 EndY=-14.5 EndZ=0
    g12: LineSegment StartX=7.75 StartY=-6 StartZ=0 EndX=7.75 EndY=-13.5 EndZ=0
    g13: LineSegment StartX=7.75 StartY=-14.5 StartZ=0 EndX=7.75 EndY=-22 EndZ=0
    g14: LineSegment StartX=6.75 StartY=-13.5 StartZ=0 EndX=7.75 EndY=-14.5 EndZ=0
    g15: LineSegment StartX=7.75 StartY=-13.5 StartZ=0 EndX=6.75 EndY=-14.5 EndZ=0
    g16: GeomPoint X=7.25 Y=-14 Z=0
  constraints (46):
    c: Coincident(g0,g1)
    c: Coincident(g1,g2)
    c: Coincident(g2,g3)
    c: Coincident(g3,g0)
    c: Horizontal(g0)
    c: Horizontal(g2)
    c: Vertical(g1)
    c: Vertical(g3)
    c: Coincident(g4,g5)
    c: Coincident(g5,g6)
    c: Coincident(g6,g7)
    c: Coincident(g7,g4)
    c: Horizontal(g4)
    c: Horizontal(g6)
    c: Vertical(g5)
    c: Vertical(g7)
    c: Coincident(g8,g9)
    c: Coincident(g9,g10)
    c: Coincident(g10,g11)
    c: Coincident(g11,g8)
    c: Horizontal(g8)
    c: Horizontal(g10)
    c: Vertical(g9)
    c: Vertical(g11)
    c: Equal(g1,g11)
    c: Equal(g11,g7)
    c: Equal(g6,g10)
    c: Equal(g10,g0)
    c: Coincident(g12,g1)
    c: Coincident(g12,g10)
    c: Vertical(g12)
    c: Coincident(g13,g8)
    c: Coincident(g13,g6)
    c: Vertical(g13)
    c: Equal(g13,g12)
    c: Coincident(g14,g8)
    c: Coincident(g15,g10)
    c: Coincident(g15,g8)
    c: PointOnObject(g16,g14)
    c: PointOnObject(g16,g15)
    c: Coincident(g9,g14)
    c: DistanceY(g16) = -14
    c: DistanceY(g1,g1) = 1
    c: DistanceX(g0,g0) = 1
    c: DistanceY(g12,g12) = 7.5
    c: DistanceX(g-1,g4) = 7.75
FEATURE [PartDesign::Pocket] Pocket021
  BaseFeature = -> Pocket019
  Direction = (0,1,2e-16)
  Length = 2
  Length2 = 5
  Profile = -> Sketch037
  ReferenceAxis = -> Sketch037 [N_Axis]
  Type = 0
FEATURE [PartDesign::Mirrored] Mirrored004
  BaseFeature = -> Pocket021
  MirrorPlane = -> Sketch037 [V_Axis]
  Originals = -> [Pocket021]
  Refine = true
FEATURE [PartDesign::Fillet] Fillet003
  Base = -> Mirrored004 [Edge70,Edge45]
  BaseFeature = -> Mirrored004
  Radius = 0.5
  SupportTransform = false
  UseAllEdges = false
FEATURE [PartDesign::Body] Body006  label="USB-Female_Bot"
  BaseFeature = -> Body
  Group = -> [Clone005,Sketch032,Pocket019,Sketch037,Pocket021,Mirrored004,Fillet003]
  Origin = -> Origin034
  Placement = pos=(18,0,0) rot=(0,0,1;0rad)
  Tip = -> Fillet003
COMPONENT P2 — recipe-attached ("USB-Female_Top", modeled in this document).
Construction recipe (the document's own serialized feature program — sketch geometry with constraints, then the solid features built on it; lengths are millimeters unless a unit is written):

FEATURE [Sketcher::SketchObject] Sketch033
  FullyConstrained = true
  MapMode = 5
  Placement = pos=(0,0,0) rot=(0.57735,0.57735,0.57735;2.0944rad)
  Support = -> [YZ_Plane035]
  sketch-geometry (8):
    g0: LineSegment StartX=-0.2 StartY=-25.2 StartZ=0 EndX=-8.2 EndY=-25.2 EndZ=0
    g1: LineSegment StartX=-8.2 StartY=-25.2 StartZ=0 EndX=-8.2 EndY=-5.2 EndZ=0
    g2: LineSegment StartX=-8.2 StartY=-5.2 StartZ=0 EndX=-0.2 EndY=-5.2 EndZ=0
    g3: LineSegment StartX=-0.2 StartY=-5.2 StartZ=0 EndX=-0.2 EndY=-25.2 EndZ=0
    g4: LineSegment StartX=-10 StartY=0 StartZ=0 EndX=10 EndY=0 EndZ=0
    g5: LineSegment StartX=10 StartY=0 StartZ=0 EndX=10 EndY=-30 EndZ=0
    g6: LineSegment StartX=10 StartY=-30 StartZ=0 EndX=-10 EndY=-30 EndZ=0
    g7: LineSegment StartX=-10 StartY=-30 StartZ=0 EndX=-10 EndY=0 EndZ=0
  constraints (23):
    c: Coincident(g0,g1)
    c: Coincident(g1,g2)
    c: Coincident(g2,g3)
    c: Coincident(g3,g0)
    c: Horizontal(g0)
    c: Horizontal(g2)
    c: Vertical(g1)
    c: Vertical(g3)
    c: DistanceY(g1,g-1) = 5.2
    c: DistanceY(g1,g1) = 20
    c: Coincident(g4,g5)
    c: Coincident(g5,g6)
    c: Coincident(g6,g7)
    c: Coincident(g7,g4)
    c: Horizontal(g4)
    c: Horizontal(g6)
    c: Vertical(g5)
    c: Vertical(g7)
    c: DistanceX(g0,g0) = 8
    c: Symmetric(g4,g4,g-1)
    c: DistanceX(g4,g4) = 20
    c: DistanceX(g2) = -0.2
    c: DistanceY(g5,g5) = 30
FEATURE [PartDesign::FeatureBase] Clone006
  BaseFeature = -> Body
FEATURE [Sketcher::SketchObject] Sketch038
  AttachmentOffset = pos=(0,0,0.2) rot=(0,0,1;0rad)
  FullyConstrained = true
  MapMode = 5
  Placement = pos=(0,-0.2,0) rot=(1,0,0;1.5708rad)
  Support = -> [XZ_Plane035]
  sketch-geometry (17):
    g0: LineSegment StartX=6.75 StartY=-5 StartZ=0 EndX=7.75 EndY=-5 EndZ=0
    g1: LineSegment StartX=7.75 StartY=-5 StartZ=0 EndX=7.75 EndY=-6 EndZ=0
    g2: LineSegment StartX=7.75 StartY=-6 StartZ=0 EndX=6.75 EndY=-6 EndZ=0
    g3: LineSegment StartX=6.75 StartY=-6 StartZ=0 EndX=6.75 EndY=-5 EndZ=0
    g4: LineSegment StartX=7.75 StartY=-23 StartZ=0 EndX=6.75 EndY=-23 EndZ=0
    g5: LineSegment StartX=6.75 StartY=-23 StartZ=0 EndX=6.75 EndY=-22 EndZ=0
    g6: LineSegment StartX=6.75 StartY=-22 StartZ=0 EndX=7.75 EndY=-22 EndZ=0
    g7: LineSegment StartX=7.75 StartY=-22 StartZ=0 EndX=7.75 EndY=-23 EndZ=0
    g8: LineSegment StartX=7.75 StartY=-14.5 StartZ=0 EndX=6.75 EndY=-14.5 EndZ=0
    g9: LineSegment StartX=6.75 StartY=-14.5 StartZ=0 EndX=6.75 EndY=-13.5 EndZ=0
    g10: LineSegment StartX=6.75 StartY=-13.5 StartZ=0 EndX=7.75 EndY=-13.5 EndZ=0
    g11: LineSegment StartX=7.75 StartY=-13.5 StartZ=0 EndX=7.75 EndY=-14.5 EndZ=0
    g12: LineSegment StartX=7.75 StartY=-6 StartZ=0 EndX=7.75 EndY=-13.5 EndZ=0
    g13: LineSegment StartX=7.75 StartY=-14.5 StartZ=0 EndX=7.75 EndY=-22 EndZ=0
    g14: LineSegment StartX=6.75 StartY=-13.5 StartZ=0 EndX=7.75 EndY=-14.5 EndZ=0
    g15: LineSegment StartX=7.75 StartY=-13.5 StartZ=0 EndX=6.75 EndY=-14.5 EndZ=0
    g16: GeomPoint X=7.25 Y=-14 Z=0
  constraints (46):
    c: Coincident(g0,g1)
    c: Coincident(g1,g2)
    c: Coincident(g2,g3)
    c: Coincident(g3,g0)
    c: Horizontal(g0)
    c: Horizontal(g2)
    c: Vertical(g1)
    c: Vertical(g3)
    c: Coincident(g4,g5)
    c: Coincident(g5,g6)
    c: Coincident(g6,g7)
    c: Coincident(g7,g4)
    c: Horizontal(g4)
    c: Horizontal(g6)
    c: Vertical(g5)
    c: Vertical(g7)
    c: Coincident(g8,g9)
    c: Coincident(g9,g10)
    c: Coincident(g10,g11)
    c: Coincident(g11,g8)
    c: Horizontal(g8)
    c: Horizontal(g10)
    c: Vertical(g9)
    c: Vertical(g11)
    c: Equal(g1,g11)
    c: Equal(g11,g7)
    c: Equal(g6,g10)
    c: Equal(g10,g0)
    c: Coincident(g12,g1)
    c: Coincident(g12,g10)
    c: Vertical(g12)
    c: Coincident(g13,g8)
    c: Coincident(g13,g6)
    c: Vertical(g13)
    c: Equal(g13,g12)
    c: Coincident(g14,g8)
    c: Coincident(g15,g10)
    c: Coincident(g15,g8)
    c: PointOnObject(g16,g14)
    c: PointOnObject(g16,g15)
    c: Coincident(g9,g14)
    c: DistanceY(g16) = -14
    c: DistanceY(g1,g1) = 1
    c: DistanceX(g0,g0) = 1
    c: DistanceY(g12,g12) = 7.5
    c: DistanceX(g-1,g4) = 7.75
FEATURE [PartDesign::Pocket] Pocket025
  BaseFeature = -> Clone006
  Direction = (-1,2e-16,-3e-16)
  Length = 21
  Length2 = 5
  Midplane = true
  Profile = -> Sketch033
  ReferenceAxis = -> Sketch033 [N_Axis]
  Type = 1
FEATURE [PartDesign::Pad] Pad014
  BaseFeature = -> Pocket025
  Direction = (0,-1,-2e-16)
  Length = 1.5
  Length2 = 10
  Profile = -> Sketch038
  ReferenceAxis = -> Sketch038 [N_Axis]
  Reversed = true
  Type = 0
FEATURE [PartDesign::Pocket] Pocket026
  BaseFeature = -> Pad014
  Direction = (-1,0,0)
  Length = 0.2
  Length2 = 5
  Profile = -> Pad014 [Face44,Face46,Face48]
  Type = 0
FEATURE [PartDesign::Pocket] Pocket027
  BaseFeature = -> Pocket026
  Direction = (0,2e-16,-1)
  Length = 0.2
  Length2 = 5
  Profile = -> Pocket026 [Face70]
  Refine = true
  Type = 0
FEATURE [PartDesign::Fillet] Fillet
  Base = -> Pocket027 [Edge225]
  BaseFeature = -> Pocket027
  Radius = 0.5
  SupportTransform = false
  UseAllEdges = false
FEATURE [PartDesign::Mirrored] Mirrored005
  BaseFeature = -> Fillet
  MirrorPlane = -> Sketch038 [V_Axis]
  Originals = -> [Pad014,Pocket026,Pocket027,Fillet]
FEATURE [PartDesign::Body] Body007  label="USB-Female_Top"
  BaseFeature = -> Body
  Group = -> [Clone006,Sketch033,Pocket025,Sketch038,Pad014,Pocket026,Pocket027,Fillet,Mirrored005]
  Origin = -> Origin035
  Placement = pos=(18,0,0) rot=(0,0,1;0rad)
  Tip = -> Mirrored005
COMPONENT P3 — geometry summary ("USB-Male-Guts"; no construction recipe available for this part):
  bounding box: 15.1 x 12.5 x 7.1 mm
  tessellated surface: 5,352 triangles
  volume: 538 mm^3 (40% of its bounding box)
  symmetry: mirror-symmetric across its x mid-plane
COMPONENT P4 — recipe-attached ("USB-Male_Bot", modeled in this document).
Construction recipe (the document's own serialized feature program — sketch geometry with constraints, then the solid features built on it; lengths are millimeters unless a unit is written):

FEATURE [PartDesign::FeatureBase] Clone011
  BaseFeature = -> Conn_Male002
FEATURE [Sketcher::SketchObject] Sketch054
  FullyConstrained = false
  MapMode = 5
  Placement = pos=(0,0,0) rot=(0.57735,0.57735,0.57735;2.0944rad)
  Support = -> [YZ_Plane042]
  sketch-geometry (4):
    g0: LineSegment StartX=-7.578 StartY=-4.2 StartZ=0 EndX=0 EndY=-4.2 EndZ=0
    g1: LineSegment StartX=0 StartY=-4.2 StartZ=0 EndX=0 EndY=-30.7458 EndZ=0
    g2: LineSegment StartX=0 StartY=-30.7458 StartZ=0 EndX=-7.578 EndY=-30.7458 EndZ=0
    g3: LineSegment StartX=-7.578 StartY=-30.7458 StartZ=0 EndX=-7.578 EndY=-4.2 EndZ=0
  constraints (10):
    c: Coincident(g0,g1)
    c: Coincident(g1,g2)
    c: Coincident(g2,g3)
    c: Coincident(g3,g0)
    c: Horizontal(g0)
    c: Horizontal(g2)
    c: Vertical(g1)
    c: Vertical(g3)
    c: PointOnObject(g1,g-2)
    c: DistanceY(g0) = -4.2
FEATURE [PartDesign::Pocket] Pocket038
  BaseFeature = -> Clone011
  Direction = (-1,2e-16,-3e-16)
  Length = 5
  Length2 = 5
  Midplane = true
  Profile = -> Sketch054
  ReferenceAxis = -> Sketch054 [N_Axis]
  Refine = true
  Type = 1
FEATURE [PartDesign::Fillet] Fillet005
  Base = -> Pocket038 [Edge84,Edge30]
  BaseFeature = -> Pocket038
  Radius = 0.5
  SupportTransform = false
  UseAllEdges = false
FEATURE [Sketcher::SketchObject] Sketch055
  FullyConstrained = true
  MapMode = 5
  Placement = pos=(0,0,0) rot=(1,0,0;1.5708rad)
  Support = -> [XZ_Plane042]
  sketch-geometry (8):
    g0: LineSegment StartX=6.25 StartY=-5.3 StartZ=0 EndX=7.75 EndY=-5.3 EndZ=0
    g1: LineSegment StartX=7.75 StartY=-5.3 StartZ=0 EndX=7.75 EndY=-6.8 EndZ=0
    g2: LineSegment StartX=7.75 StartY=-6.8 StartZ=0 EndX=6.25 EndY=-6.8 EndZ=0
    g3: LineSegment StartX=6.25 StartY=-6.8 StartZ=0 EndX=6.25 EndY=-5.3 EndZ=0
    g4: LineSegment StartX=6.25 StartY=-11.8 StartZ=0 EndX=7.75 EndY=-11.8 EndZ=0
    g5: LineSegment StartX=7.75 StartY=-11.8 StartZ=0 EndX=7.75 EndY=-13.3 EndZ=0
    g6: LineSegment StartX=7.75 StartY=-13.3 StartZ=0 EndX=6.25 EndY=-13.3 EndZ=0
    g7: LineSegment StartX=6.25 StartY=-13.3 StartZ=0 EndX=6.25 EndY=-11.8 EndZ=0
  constraints (24):
    c: Coincident(g0,g1)
    c: Coincident(g1,g2)
    c: Coincident(g2,g3)
    c: Coincident(g3,g0)
    c: Horizontal(g0)
    c: Horizontal(g2)
    c: Vertical(g1)
    c: Vertical(g3)
    c: Coincident(g4,g5)
    c: Coincident(g5,g6)
    c: Coincident(g6,g7)
    c: Coincident(g7,g4)
    c: Horizontal(g4)
    c: Horizontal(g6)
    c: Vertical(g5)
    c: Vertical(g7)
    c: Equal(g5,g4)
    c: Equal(g1,g2)
    c: Vertical(g4,g1)
    c: Equal(g5,g1)
    c: DistanceY(g3,g3) = 1.5
    c: DistanceX(g0) = 7.75
    c: DistanceY(g4,g1) = 5
    c: DistanceY(g5) = -13.3
FEATURE [PartDesign::Pocket] Pocket039
  BaseFeature = -> Fillet005
  Direction = (0,1,-2e-16)
  Length = 2
  Length2 = 5
  Profile = -> Sketch055
  ReferenceAxis = -> Sketch055 [N_Axis]
  Type = 0
FEATURE [PartDesign::Mirrored] Mirrored010
  BaseFeature = -> Pocket039
  MirrorPlane = -> Sketch055 [V_Axis]
  Originals = -> [Pocket039]
FEATURE [PartDesign::Body] Body012  label="USB-Male_Bot"
  Group = -> [Clone011,Sketch054,Pocket038,Fillet005,Sketch055,Pocket039,Mirrored010]
  Origin = -> Origin042
  Placement = pos=(-18,0,0) rot=(0,0,1;0rad)
  Tip = -> Mirrored010
COMPONENT P5 — recipe-attached ("USB_Male_Top", modeled in this document).
Construction recipe (the document's own serialized feature program — sketch geometry with constraints, then the solid features built on it; lengths are millimeters unless a unit is written):

FEATURE [PartDesign::FeatureBase] Clone012
  BaseFeature = -> Conn_Male002
FEATURE [Sketcher::SketchObject] Sketch056
  FullyConstrained = false
  MapMode = 5
  Placement = pos=(0,0,0) rot=(0.57735,0.57735,0.57735;2.0944rad)
  Support = -> [YZ_Plane043]
  expr: Constraints[8] = -4.2 - 0.2
  sketch-geometry (8):
    g0: LineSegment StartX=-7.2 StartY=-4.4 StartZ=0 EndX=-0.2 EndY=-4.4 EndZ=0
    g1: LineSegment StartX=-0.2 StartY=-4.4 StartZ=0 EndX=-0.2 EndY=-26.4 EndZ=0
    g2: LineSegment StartX=-0.2 StartY=-26.4 StartZ=0 EndX=-7.2 EndY=-26.4 EndZ=0
    g3: LineSegment StartX=-7.2 StartY=-26.4 StartZ=0 EndX=-7.2 EndY=-4.4 EndZ=0
    g4: LineSegment StartX=-13.8934 StartY=6.39114 StartZ=0 EndX=12.459 EndY=6.39114 EndZ=0
    g5: LineSegment StartX=12.459 StartY=6.39114 StartZ=0 EndX=12.459 EndY=-32.2298 EndZ=0
    g6: LineSegment StartX=12.459 StartY=-32.2298 StartZ=0 EndX=-13.8934 EndY=-32.2298 EndZ=0
    g7: LineSegment StartX=-13.8934 StartY=-32.2298 StartZ=0 EndX=-13.8934 EndY=6.39114 EndZ=0
  constraints (20):
    c: Coincident(g0,g1)
    c: Coincident(g1,g2)
    c: Coincident(g2,g3)
    c: Coincident(g3,g0)
    c: Horizontal(g0)
    c: Horizontal(g2)
    c: Vertical(g1)
    c: Vertical(g3)
    c: DistanceY(g0) = -4.4
    c: DistanceX(g1) = -0.2
    c: DistanceY(g3,g3) = 22
    c: DistanceX(g2,g2) = 7
    c: Coincident(g4,g5)
    c: Coincident(g5,g6)
    c: Coincident(g6,g7)
    c: Coincident(g7,g4)
    c: Horizontal(g4)
    c: Horizontal(g6)
    c: Vertical(g5)
    c: Vertical(g7)
FEATURE [PartDesign::Pocket] Pocket040
  BaseFeature = -> Clone012
  Direction = (-1,2e-16,-3e-16)
  Length = 5
  Length2 = 5
  Midplane = true
  Profile = -> Sketch056
  ReferenceAxis = -> Sketch056 [N_Axis]
  Type = 1
FEATURE [Sketcher::SketchObject] Sketch057
  AttachmentOffset = pos=(0,0,0.2) rot=(0,0,1;0rad)
  FullyConstrained = true
  MapMode = 5
  Placement = pos=(0,-0.2,0) rot=(1,0,0;1.5708rad)
  Support = -> [XZ_Plane043]
  sketch-geometry (8):
    g0: LineSegment StartX=6.25 StartY=-5.3 StartZ=0 EndX=7.75 EndY=-5.3 EndZ=0
    g1: LineSegment StartX=7.75 StartY=-5.3 StartZ=0 EndX=7.75 EndY=-6.8 EndZ=0
    g2: LineSegment StartX=7.75 StartY=-6.8 StartZ=0 EndX=6.25 EndY=-6.8 EndZ=0
    g3: LineSegment StartX=6.25 StartY=-6.8 StartZ=0 EndX=6.25 EndY=-5.3 EndZ=0
    g4: LineSegment StartX=6.25 StartY=-11.8 StartZ=0 EndX=7.75 EndY=-11.8 EndZ=0
    g5: LineSegment StartX=7.75 StartY=-11.8 StartZ=0 EndX=7.75 EndY=-13.3 EndZ=0
    g6: LineSegment StartX=7.75 StartY=-13.3 StartZ=0 EndX=6.25 EndY=-13.3 EndZ=0
    g7: LineSegment StartX=6.25 StartY=-13.3 StartZ=0 EndX=6.25 EndY=-11.8 EndZ=0
  constraints (24):
    c: Coincident(g0,g1)
    c: Coincident(g1,g2)
    c: Coincident(g2,g3)
    c: Coincident(g3,g0)
    c: Horizontal(g0)
    c: Horizontal(g2)
    c: Vertical(g1)
    c: Vertical(g3)
    c: Coincident(g4,g5)
    c: Coincident(g5,g6)
    c: Coincident(g6,g7)
    c: Coincident(g7,g4)
    c: Horizontal(g4)
    c: Horizontal(g6)
    c: Vertical(g5)
    c: Vertical(g7)
    c: Equal(g5,g4)
    c: Equal(g1,g2)
    c: Vertical(g4,g1)
    c: Equal(g5,g1)
    c: DistanceY(g3,g3) = 1.5
    c: DistanceX(g0) = 7.75
    c: DistanceY(g4,g1) = 5
    c: DistanceY(g5) = -13.3
FEATURE [PartDesign::Fillet] Fillet006
  Base = -> Pocket040 [Edge31,Edge25]
  BaseFeature = -> Pocket040
  Radius = 0.5
  SupportTransform = false
  UseAllEdges = false
FEATURE [PartDesign::Pad] Pad025
  BaseFeature = -> Fillet006
  Direction = (0,-1,2e-16)
  Length = 1.5
  Length2 = 10
  Profile = -> Sketch057
  ReferenceAxis = -> Sketch057 [N_Axis]
  Reversed = true
  Type = 0
FEATURE [PartDesign::Mirrored] Mirrored011
  BaseFeature = -> Pad025
  MirrorPlane = -> Sketch057 [V_Axis]
  Originals = -> [Pad025]
  Refine = true
FEATURE [PartDesign::Pocket] Pocket041
  BaseFeature = -> Mirrored011
  Direction = (1,0,0)
  Length = 0.2
  Length2 = 5
  Profile = -> Mirrored011 [Face46,Face44,Face13,Face15]
  Refine = true
  Type = 0
FEATURE [PartDesign::Body] Body013  label="USB_Male_Top"
  Group = -> [Clone012,Sketch056,Pocket040,Sketch057,Fillet006,Pad025,Mirrored011,Pocket041]
  Origin = -> Origin043
  Placement = pos=(-18,0,0) rot=(0,0,1;0rad)
  Tip = -> Pocket041
COMPONENT P6 — recipe-attached ("Housing-USB_Male", modeled in this document).
Construction recipe (the document's own serialized feature program — sketch geometry with constraints, then the solid features built on it; lengths are millimeters unless a unit is written):

FEATURE [PartDesign::CoordinateSystem] LCS_002
  AttacherType = Attacher::AttachEngine3D
  MapMode = 2
  Support = -> [X_Axis008]
FEATURE [Sketcher::SketchObject] Sketch013
  FullyConstrained = true
  MapMode = 5
  Support = -> [XY_Plane008]
  sketch-geometry (8):
    g0: LineSegment StartX=-6.75 StartY=4.75 StartZ=0 EndX=6.75 EndY=4.75 EndZ=0
    g1: LineSegment StartX=8.75 StartY=2.75 StartZ=0 EndX=8.75 EndY=-2.75 EndZ=0
    g2: LineSegment StartX=6.75 StartY=-4.75 StartZ=0 EndX=-6.75 EndY=-4.75 EndZ=0
    g3: LineSegment StartX=-8.75 StartY=-2.75 StartZ=0 EndX=-8.75 EndY=2.75 EndZ=0
    g4: ArcOfCircle CenterX=6.75 CenterY=2.75 CenterZ=0 NormalX=0 NormalY=0 NormalZ=1 AngleXU=0 Radius=2 StartAngle=4.675e-13 EndAngle=1.5708
    g5: ArcOfCircle CenterX=6.75 CenterY=-2.75 CenterZ=0 NormalX=0 NormalY=0 NormalZ=1 AngleXU=0 Radius=2 StartAngle=4.71239 EndAngle=6.28319
    g6: ArcOfCircle CenterX=-6.75 CenterY=-2.75 CenterZ=0 NormalX=0 NormalY=0 NormalZ=1 AngleXU=0 Radius=2 StartAngle=3.14159 EndAngle=4.71239
    g7: ArcOfCircle CenterX=-6.75 CenterY=2.75 CenterZ=0 NormalX=0 NormalY=0 NormalZ=1 AngleXU=0 Radius=2 StartAngle=1.5708 EndAngle=3.14159
  constraints (19):
    c: Horizontal(g0)
    c: Horizontal(g2)
    c: Vertical(g1)
    c: Vertical(g3)
    c: Tangent(g0,g4) = 1.5708
    c: Tangent(g1,g4) = 1.5708
    c: Tangent(g1,g5) = 1.5708
    c: Tangent(g2,g5) = 1.5708
    c: Tangent(g2,g6) = 1.5708
    c: Tangent(g3,g6) = 1.5708
    c: Tangent(g0,g7) = 1.5708
    c: Tangent(g3,g7) = 1.5708
    c: Equal(g7,g6)
    c: Equal(g6,g5)
    c: Equal(g5,g4)
    c: Symmetric(g7,g5,g-1)
    c: DistanceY(g2,g0) = 9.5
    c: DistanceX(g3,g1) = 17.5
    c: Radius(g4) = 2
FEATURE [PartDesign::Pad] Pad005
  Direction = (0,0,1)
  Length = 25
  Length2 = 10
  Profile = -> Sketch013
  ReferenceAxis = -> Sketch013 [N_Axis]
  Reversed = true
  Type = 0
FEATURE [Sketcher::SketchObject] Sketch014
  FullyConstrained = true
  MapMode = 5
  Support = -> [Pad005]
  expr: Constraints[19] = 3.1 mm
  expr: Constraints[20] = 11.2 - 2
  sketch-geometry (8):
    g0: LineSegment StartX=4.6 StartY=1.55 StartZ=0 EndX=7.7 EndY=1.55 EndZ=0
    g1: LineSegment StartX=7.7 StartY=1.55 StartZ=0 EndX=7.7 EndY=-1.55 EndZ=0
    g2: LineSegment StartX=7.7 StartY=-1.55 StartZ=0 EndX=4.6 EndY=-1.55 EndZ=0
    g3: LineSegment StartX=4.6 StartY=-1.55 StartZ=0 EndX=4.6 EndY=1.55 EndZ=0
    g4: LineSegment StartX=-7.7 StartY=1.55 StartZ=0 EndX=-4.6 EndY=1.55 EndZ=0
    g5: LineSegment StartX=-4.6 StartY=1.55 StartZ=0 EndX=-4.6 EndY=-1.55 EndZ=0
    g6: LineSegment StartX=-4.6 StartY=-1.55 StartZ=0 EndX=-7.7 EndY=-1.55 EndZ=0
    g7: LineSegment StartX=-7.7 StartY=-1.55 StartZ=0 EndX=-7.7 EndY=1.55 EndZ=0
  constraints (21):
    c: Coincident(g0,g1)
    c: Coincident(g1,g2)
    c: Coincident(g2,g3)
    c: Coincident(g3,g0)
    c: Horizontal(g0)
    c: Horizontal(g2)
    c: Vertical(g1)
    c: Coincident(g4,g5)
    c: Coincident(g5,g6)
    c: Coincident(g6,g7)
    c: Coincident(g7,g4)
    c: Horizontal(g4)
    c: Horizontal(g6)
    c: Vertical(g7)
    c: Equal(g5,g4)
    c: Equal(g4,g0)
    c: Symmetric(g2,g0,g-1)
    c: Symmetric(g5,g4,g-1)
    c: Symmetric(g4,g0,g-2)
    c: DistanceX(g0,g0) = 3.1
    c: DistanceX(g4,g0) = 9.2
FEATURE [PartDesign::Pocket] Pocket008  label="magnets001"
  BaseFeature = -> Pad005
  Direction = (0,0,-1)
  Length = 3.2
  Length2 = 5
  Profile = -> Sketch014
  ReferenceAxis = -> Sketch014 [N_Axis]
  Type = 0
FEATURE [Sketcher::SketchObject] Sketch017
  AttachmentOffset = pos=(0,0,-4.2) rot=(0,0,1;0rad)
  FullyConstrained = true
  MapMode = 5
  Placement = pos=(0,0,-4.2) rot=(0,0,1;0rad)
  Support = -> [XY_Plane008]
  expr: Constraints[16] = 9.5 - 2
  expr: Constraints[17] = 17.5 - 2
  sketch-geometry (8):
    g0: LineSegment StartX=-6.75 StartY=3.75 StartZ=0 EndX=6.75 EndY=3.75 EndZ=0
    g1: LineSegment StartX=7.75 StartY=2.75 StartZ=0 EndX=7.75 EndY=-2.75 EndZ=0
    g2: LineSegment StartX=6.75 StartY=-3.75 StartZ=0 EndX=-6.75 EndY=-3.75 EndZ=0
    g3: LineSegment StartX=-7.75 StartY=-2.75 StartZ=0 EndX=-7.75 EndY=2.75 EndZ=0
    g4: ArcOfCircle CenterX=6.75 CenterY=2.75 CenterZ=0 NormalX=0 NormalY=0 NormalZ=1 AngleXU=0 Radius=1 StartAngle=0 EndAngle=1.5708
    g5: ArcOfCircle CenterX=6.75 CenterY=-2.75 CenterZ=0 NormalX=0 NormalY=0 NormalZ=1 AngleXU=0 Radius=1 StartAngle=4.71239 EndAngle=6.28319
    g6: ArcOfCircle CenterX=-6.75 CenterY=-2.75 CenterZ=0 NormalX=0 NormalY=0 NormalZ=1 AngleXU=0 Radius=1 StartAngle=3.14159 EndAngle=4.71239
    g7: ArcOfCircle CenterX=-6.75 CenterY=2.75 CenterZ=0 NormalX=0 NormalY=0 NormalZ=1 AngleXU=0 Radius=1 StartAngle=1.5708 EndAngle=3.14159
  constraints (19):
    c: Horizontal(g0)
    c: Horizontal(g2)
    c: Vertical(g1)
    c: Vertical(g3)
    c: Tangent(g0,g4) = 1.5708
    c: Tangent(g1,g4) = 1.5708
    c: Tangent(g1,g5) = 1.5708
    c: Tangent(g2,g5) = 1.5708
    c: Tangent(g2,g6) = 1.5708
    c: Tangent(g3,g6) = 1.5708
    c: Tangent(g0,g7) = 1.5708
    c: Tangent(g3,g7) = 1.5708
    c: Equal(g7,g6)
    c: Equal(g6,g5)
    c: Equal(g5,g4)
    c: Symmetric(g7,g5,g-1)
    c: DistanceY(g2,g0) = 7.5
    c: DistanceX(g3,g1) = 15.5
    c: Radius(g4) = 1
FEATURE [PartDesign::Pocket] Pocket010  label="thickness"
  BaseFeature = -> Pocket008
  Direction = (0,0,-1)
  Length = 5
  Length2 = 5
  Profile = -> Sketch017
  ReferenceAxis = -> Sketch017 [N_Axis]
  Type = 1
FEATURE [Sketcher::SketchObject] Sketch018
  AttachmentOffset = pos=(0,0,4.75) rot=(0,0,1;0rad)
  FullyConstrained = false
  MapMode = 5
  Placement = pos=(0,-4.75,-1.1e-15) rot=(1,0,0;1.5708rad)
  Support = -> [XZ_Plane008]
  sketch-geometry (6):
    g0: LineSegment StartX=1.08462 StartY=-1.5 StartZ=0 EndX=-1.08462 EndY=-1.5 EndZ=0
    g1: LineSegment StartX=-1.30113 StartY=-1.875 StartZ=0 EndX=-0.216506 EndY=-3.75362 EndZ=0
    g2: LineSegment StartX=0.216506 StartY=-3.75362 StartZ=0 EndX=1.30113 EndY=-1.875 EndZ=0
    g3: ArcOfCircle CenterX=1.08462 CenterY=-1.75 CenterZ=0 NormalX=0 NormalY=0 NormalZ=1 AngleXU=0 Radius=0.25 StartAngle=5.75959 EndAngle=7.85398
    g4: ArcOfCircle CenterX=-1.08462 CenterY=-1.75 CenterZ=0 NormalX=0 NormalY=0 NormalZ=1 AngleXU=0 Radius=0.25 StartAngle=1.5708 EndAngle=3.66519
    g5: ArcOfCircle CenterX=1e-16 CenterY=-3.62862 CenterZ=0 NormalX=0 NormalY=0 NormalZ=1 AngleXU=0 Radius=0.25 StartAngle=3.66519 EndAngle=5.75959
  constraints (13):
    c: Tangent(g0,g3) = -1.5708
    c: Tangent(g2,g3) = -1.5708
    c: Tangent(g0,g4) = -1.5708
    c: Tangent(g1,g4) = -1.5708
    c: Tangent(g1,g5) = -1.5708
    c: Tangent(g2,g5) = -1.5708
    c: Equal(g3,g4)
    c: Equal(g4,g5)
    c: Radius(g3) = 0.25
    c: Symmetric(g0,g0,g-2)
    c: Equal(g0,g1)
    c: Equal(g1,g2)
    c: DistanceY(g0) = -1.5
FEATURE [PartDesign::Pocket] Pocket011  label="sign"
  BaseFeature = -> Pocket010
  Direction = (0,1,2e-16)
  Length = 0.5
  Length2 = 5
  Profile = -> Sketch018
  ReferenceAxis = -> Sketch018 [N_Axis]
  Type = 0
FEATURE [PartDesign::Chamfer] Chamfer002
  Angle = 45
  Base = -> Pocket011 [Edge12]
  BaseFeature = -> Pocket011
  ChamferType = 0
  FlipDirection = false
  Size = 0.5
  Size2 = 1
  SupportTransform = false
  UseAllEdges = false
FEATURE [Sketcher::SketchObject] Sketch019
  FullyConstrained = true
  MapMode = 5
  Support = -> [Chamfer002]
  expr: Constraints[5] = (9.2 + 3) / 2
  sketch-geometry (5):
    g0: Circle CenterX=0 CenterY=-1.5 CenterZ=0 NormalX=0 NormalY=0 NormalZ=1 AngleXU=0 Radius=0.75
    g1: Circle CenterX=2.9 CenterY=-1.5 CenterZ=0 NormalX=0 NormalY=0 NormalZ=1 AngleXU=0 Radius=0.75
    g2: Circle CenterX=-2.9 CenterY=-1.5 CenterZ=0 NormalX=0 NormalY=0 NormalZ=1 AngleXU=0 Radius=0.75
    g3: Circle CenterX=-6.1 CenterY=0 CenterZ=0 NormalX=0 NormalY=0 NormalZ=1 AngleXU=0 Radius=1
    g4: Circle CenterX=6.1 CenterY=0 CenterZ=0 NormalX=0 NormalY=0 NormalZ=1 AngleXU=0 Radius=1
  constraints (13):
    c: Equal(g1,g0)
    c: Equal(g0,g2)
    c: PointOnObject(g3,g-1)
    c: Equal(g4,g3)
    c: DistanceX(g1) = 2.9
    c: DistanceX(g4) = 6.1
    c: Diameter(g0) = 1.5
    c: Diameter(g4) = 2
    c: PointOnObject(g0,g-2)
    c: Symmetric(g1,g2,g0)
    c: DistanceY(g-1,g0) = -1.5
    c: Horizontal(g2,g1)
    c: Symmetric(g4,g3,g-1)
FEATURE [PartDesign::Pocket] Pocket012  label="pins"
  BaseFeature = -> Chamfer002
  Direction = (0,0,-1)
  Length = 5
  Length2 = 5
  Profile = -> Sketch019
  ReferenceAxis = -> Sketch019 [N_Axis]
  Type = 1
FEATURE [PartDesign::Chamfer] Chamfer003
  Angle = 45
  Base = -> Pocket012 [Edge118,Edge119,Edge39,Edge38,Edge37]
  BaseFeature = -> Pocket012
  ChamferType = 0
  FlipDirection = false
  Size = 0.25
  Size2 = 1
  SupportTransform = false
  UseAllEdges = false
FEATURE [PartDesign::CoordinateSystem] LCS_mag1
  AttacherType = Attacher::AttachEngine3D
  MapMode = 45
  Placement = pos=(-6.20221,2e-16,-3.2) rot=(0,0,1;0rad)
  Support = -> [Chamfer003]
FEATURE [PartDesign::CoordinateSystem] LCS_mag2
  AttacherType = Attacher::AttachEngine3D
  MapMode = 45
  Placement = pos=(6.20221,4e-16,-3.2) rot=(0,0,1;0rad)
  Support = -> [Chamfer003]
FEATURE [PartDesign::CoordinateSystem] LCS_pin1
  AttacherType = Attacher::AttachEngine3D
  MapMode = 45
  Placement = pos=(-2.9,-1.5,0) rot=(0,0,1.00277;0rad)
  Support = -> [Chamfer003]
FEATURE [PartDesign::CoordinateSystem] LCS_pin2
  AttacherType = Attacher::AttachEngine3D
  MapMode = 45
  Placement = pos=(4.7e-15,-1.5,0) rot=(0,0,1;0rad)
  Support = -> [Chamfer003]
FEATURE [PartDesign::CoordinateSystem] LCS_pin3
  AttacherType = Attacher::AttachEngine3D
  MapMode = 45
  Placement = pos=(2.9,-1.5,0) rot=(0,0,-1.00277;0rad)
  Support = -> [Chamfer003]
FEATURE [Sketcher::SketchObject] Sketch027
  AttachmentOffset = pos=(0,0,-25) rot=(0,0,1;0rad)
  FullyConstrained = true
  MapMode = 5
  Placement = pos=(0,0,-25) rot=(0,0,1;0rad)
  Support = -> [XY_Plane008]
  expr: Constraints[39] = 12 + 0.2
  sketch-geometry (18):
    g0: LineSegment StartX=-6.75 StartY=4.75 StartZ=0 EndX=6.75 EndY=4.75 EndZ=0
    g1: LineSegment StartX=8.75 StartY=2.75 StartZ=0 EndX=8.75 EndY=-2.75 EndZ=0
    g2: LineSegment StartX=6.75 StartY=-4.75 StartZ=0 EndX=-6.75 EndY=-4.75 EndZ=0
    g3: LineSegment StartX=-8.75 StartY=-2.75 StartZ=0 EndX=-8.75 EndY=2.75 EndZ=0
    g4: ArcOfCircle CenterX=6.75 CenterY=2.75 CenterZ=0 NormalX=0 NormalY=0 NormalZ=1 AngleXU=0 Radius=2 StartAngle=0 EndAngle=1.5708
    g5: ArcOfCircle CenterX=6.75 CenterY=-2.75 CenterZ=0 NormalX=0 NormalY=0 NormalZ=1 AngleXU=0 Radius=2 StartAngle=4.71239 EndAngle=6.28319
    g6: ArcOfCircle CenterX=-6.75 CenterY=-2.75 CenterZ=0 NormalX=0 NormalY=0 NormalZ=1 AngleXU=0 Radius=2 StartAngle=3.14159 EndAngle=4.71239
    g7: ArcOfCircle CenterX=-6.75 CenterY=2.75 CenterZ=0 NormalX=0 NormalY=0 NormalZ=1 AngleXU=0 Radius=2 StartAngle=1.5708 EndAngle=3.14159
    g8: ArcOfCircle CenterX=-5.45 CenterY=1.7 CenterZ=0 NormalX=0 NormalY=0 NormalZ=1 AngleXU=0 Radius=0.65 StartAngle=1.5708 EndAngle=3.14159
    g9: LineSegment StartX=-5.45 StartY=2.35 StartZ=0 EndX=5.45 EndY=2.35 EndZ=0
    g10: ArcOfCircle CenterX=5.45 CenterY=1.7 CenterZ=0 NormalX=0 NormalY=0 NormalZ=1 AngleXU=0 Radius=0.65 StartAngle=2e-16 EndAngle=1.5708
    g11: LineSegment StartX=6.1 StartY=1.7 StartZ=0 EndX=6.1 EndY=-1.7 EndZ=0
    g12: ArcOfCircle CenterX=5.45 CenterY=-1.7 CenterZ=0 NormalX=0 NormalY=0 NormalZ=1 AngleXU=0 Radius=0.65 StartAngle=4.71239 EndAngle=6.28319
    g13: LineSegment StartX=5.45 StartY=-2.35 StartZ=0 EndX=-5.45 EndY=-2.35 EndZ=0
    g14: ArcOfCircle CenterX=-5.45 CenterY=-1.7 CenterZ=0 NormalX=0 NormalY=0 NormalZ=1 AngleXU=0 Radius=0.65 StartAngle=3.14159 EndAngle=4.71239
    g15: LineSegment StartX=-6.1 StartY=-1.7 StartZ=0 EndX=-6.1 EndY=1.7 EndZ=0
    g16: GeomPoint X=-6.1 Y=2.35 Z=0
    g17: GeomPoint X=6.1 Y=-2.35 Z=0
  constraints (42):
    c: Horizontal(g0)
    c: Horizontal(g2)
    c: Vertical(g1)
    c: Vertical(g3)
    c: Tangent(g0,g4) = 1.5708
    c: Tangent(g1,g4) = 1.5708
    c: Tangent(g1,g5) = 1.5708
    c: Tangent(g2,g5) = 1.5708
    c: Tangent(g2,g6) = 1.5708
    c: Tangent(g3,g6) = 1.5708
    c: Tangent(g0,g7) = 1.5708
    c: Tangent(g3,g7) = 1.5708
    c: Equal(g7,g6)
    c: Equal(g6,g5)
    c: Equal(g5,g4)
    c: Symmetric(g7,g5,g-1)
    c: DistanceY(g2,g0) = 9.5
    c: DistanceX(g3,g1) = 17.5
    c: Radius(g4) = 2
    c: Tangent(g8,g9) = 1.5708
    c: Tangent(g9,g10) = 1.5708
    c: Tangent(g10,g11) = 1.5708
    c: Tangent(g11,g12) = 1.5708
    c: Tangent(g12,g13) = 1.5708
    c: Tangent(g13,g14) = 1.5708
    c: Tangent(g14,g15) = 1.5708
    c: Tangent(g15,g8) = 1.5708
    c: Horizontal(g9)
    c: Horizontal(g13)
    c: Vertical(g11)
    c: Vertical(g15)
    c: Equal(g8,g10)
    c: Equal(g10,g12)
    c: Equal(g12,g14)
    c: PointOnObject(g16,g9)
    c: PointOnObject(g16,g15)
    c: PointOnObject(g17,g11)
    c: PointOnObject(g17,g13)
    c: Symmetric(g16,g17,g-1)
    c: DistanceX(g8,g10) = 12.2
    c: DistanceY(g12,g9) = 4.7
    c: Radius(g10) = 0.65
FEATURE [PartDesign::Pad] Pad009  label="back_wall001"
  BaseFeature = -> Chamfer003
  Direction = (0,0,1)
  Length = 1
  Length2 = 10
  Profile = -> Sketch027
  ReferenceAxis = -> Sketch027 [N_Axis]
  Refine = true
  Type = 0
FEATURE [PartDesign::Chamfer] Chamfer
  Angle = 45
  Base = -> Pad009 [Edge129]
  BaseFeature = -> Pad009
  ChamferType = 0
  FlipDirection = false
  Size = 0.5
  Size2 = 1
  SupportTransform = false
  UseAllEdges = false
FEATURE [PartDesign::CoordinateSystem] LCS_bottom_edge  label="LCS_bottom_edge001"
  AttacherType = Attacher::AttachEngine3D
  MapMode = 45
  Placement = pos=(0,1e-16,-25) rot=(0,0,1;1.5708rad)
  Support = -> [Chamfer]
FEATURE [Sketcher::SketchObject] Sketch046
  AttachmentOffset = pos=(0,0,5) rot=(0,0,1;0rad)
  FullyConstrained = true
  MapMode = 5
  Placement = pos=(5,-1.1e-15,1.1e-15) rot=(0.57735,0.57735,0.57735;2.0944rad)
  Support = -> [YZ_Plane008]
  expr: Constraints[13] = 1.5 - 0.2
  expr: Constraints[15] = 10.5 + 0.2
  sketch-geometry (6):
    g0: LineSegment StartX=3.75 StartY=-24 StartZ=0 EndX=3.75 EndY=-11.8 EndZ=0
    g1: LineSegment StartX=3.75 StartY=-11.8 StartZ=0 EndX=0.05 EndY=-11.8 EndZ=0
    g2: LineSegment StartX=0.05 StartY=-11.8 StartZ=0 EndX=0.05 EndY=-13.3 EndZ=0
    g3: LineSegment StartX=0.05 StartY=-13.3 StartZ=0 EndX=2.45 EndY=-13.3 EndZ=0
    g4: LineSegment StartX=2.45 StartY=-13.3 StartZ=0 EndX=2.45 EndY=-24 EndZ=0
    g5: LineSegment StartX=2.45 StartY=-24 StartZ=0 EndX=3.75 EndY=-24 EndZ=0
  constraints (18):
    c: Vertical(g0)
    c: Coincident(g0,g1)
    c: Horizontal(g1)
    c: Coincident(g1,g2)
    c: Vertical(g2)
    c: Coincident(g2,g3)
    c: Coincident(g3,g4)
    c: Vertical(g4)
    c: Coincident(g4,g5)
    c: Coincident(g5,g0)
    c: Horizontal(g5)
    c: Horizontal(g3)
    c: DistanceX(g0) = 3.75
    c: DistanceX(g5,g5) = 1.3
    c: DistanceY(g0) = -24
    c: DistanceY(g4,g4) = 10.7
    c: DistanceY(g2,g2) = 1.5
    c: DistanceX(g1,g1) = 3.7
FEATURE [PartDesign::Pad] Pad021
  BaseFeature = -> Chamfer
  Direction = (1,-2e-16,3e-16)
  Length = 1
  Length2 = 10
  Midplane = true
  Profile = -> Sketch046
  ReferenceAxis = -> Sketch046 [N_Axis]
  Type = 0
FEATURE [PartDesign::LinearPattern] LinearPattern001
  BaseFeature = -> Pad021
  Direction = -> Sketch046 [N_Axis]
  Length = 10
  Occurrences = 4
  Originals = -> [Pad021]
  Reversed = true
FEATURE [Sketcher::SketchObject] Sketch047
  FullyConstrained = true
  MapMode = 5
  Placement = pos=(0,0,0) rot=(1,0,0;1.5708rad)
  Support = -> [XZ_Plane008]
  sketch-geometry (4):
    g0: LineSegment StartX=6.2 StartY=-13.5 StartZ=0 EndX=7.75 EndY=-13.5 EndZ=0
    g1: LineSegment StartX=7.75 StartY=-13.5 StartZ=0 EndX=7.75 EndY=-24 EndZ=0
    g2: LineSegment StartX=7.75 StartY=-24 StartZ=0 EndX=6.2 EndY=-24 EndZ=0
    g3: LineSegment StartX=6.2 StartY=-24 StartZ=0 EndX=6.2 EndY=-13.5 EndZ=0
  constraints (12):
    c: Coincident(g0,g1)
    c: Coincident(g1,g2)
    c: Coincident(g2,g3)
    c: Coincident(g3,g0)
    c: Horizontal(g0)
    c: Horizontal(g2)
    c: Vertical(g1)
    c: Vertical(g3)
    c: DistanceY(g1) = -24
    c: DistanceX(g1) = 7.75
    c: DistanceX(g2,g2) = 1.55
    c: DistanceY(g1,g1) = 10.5
FEATURE [PartDesign::Pad] Pad022
  BaseFeature = -> LinearPattern001
  Direction = (0,-1,-2e-16)
  Length = 2
  Length2 = 10
  Midplane = true
  Profile = -> Sketch047
  ReferenceAxis = -> Sketch047 [N_Axis]
  Type = 0
FEATURE [PartDesign::Mirrored] Mirrored008
  BaseFeature = -> Pad022
  MirrorPlane = -> Sketch047 [V_Axis]
  Originals = -> [Pad022]
FEATURE [Sketcher::SketchObject] Sketch048
  FullyConstrained = true
  MapMode = 5
  Placement = pos=(0,0,0) rot=(1,0,0;1.5708rad)
  Support = -> [XZ_Plane008]
  sketch-geometry (8):
    g0: LineSegment StartX=6.25 StartY=-5.3 StartZ=0 EndX=7.75 EndY=-5.3 EndZ=0
    g1: LineSegment StartX=7.75 StartY=-5.3 StartZ=0 EndX=7.75 EndY=-6.8 EndZ=0
    g2: LineSegment StartX=7.75 StartY=-6.8 StartZ=0 EndX=6.25 EndY=-6.8 EndZ=0
    g3: LineSegment StartX=6.25 StartY=-6.8 StartZ=0 EndX=6.25 EndY=-5.3 EndZ=0
    g4: LineSegment StartX=6.25 StartY=-11.8 StartZ=0 EndX=7.75 EndY=-11.8 EndZ=0
    g5: LineSegment StartX=7.75 StartY=-11.8 StartZ=0 EndX=7.75 EndY=-13.3 EndZ=0
    g6: LineSegment StartX=7.75 StartY=-13.3 StartZ=0 EndX=6.25 EndY=-13.3 EndZ=0
    g7: LineSegment StartX=6.25 StartY=-13.3 StartZ=0 EndX=6.25 EndY=-11.8 EndZ=0
  constraints (24):
    c: Coincident(g0,g1)
    c: Coincident(g1,g2)
    c: Coincident(g2,g3)
    c: Coincident(g3,g0)
    c: Horizontal(g0)
    c: Horizontal(g2)
    c: Vertical(g1)
    c: Vertical(g3)
    c: Coincident(g4,g5)
    c: Coincident(g5,g6)
    c: Coincident(g6,g7)
    c: Coincident(g7,g4)
    c: Horizontal(g4)
    c: Horizontal(g6)
    c: Vertical(g5)
    c: Vertical(g7)
    c: Equal(g5,g4)
    c: Equal(g1,g2)
    c: Vertical(g4,g1)
    c: Equal(g5,g1)
    c: DistanceY(g3,g3) = 1.5
    c: DistanceX(g0) = 7.75
    c: DistanceY(g4,g1) = 5
    c: DistanceY(g5) = -13.3
FEATURE [PartDesign::Pad] Pad023
  BaseFeature = -> Mirrored008
  Direction = (0,-1,-2e-16)
  Length = 8
  Length2 = 10
  Midplane = true
  Profile = -> Sketch048
  ReferenceAxis = -> Sketch048 [N_Axis]
  Type = 0
FEATURE [PartDesign::Mirrored] Mirrored009
  BaseFeature = -> Pad023
  MirrorPlane = -> Sketch048 [V_Axis]
  Originals = -> [Pad023]
FEATURE [Sketcher::SketchObject] Sketch049
  AttachmentOffset = pos=(0,0,3.55) rot=(0,0,1;0rad)
  FullyConstrained = true
  MapMode = 5
  Placement = pos=(0,-3.55,8e-16) rot=(1,0,0;1.5708rad)
  Support = -> [XZ_Plane040]
  expr: .AttachmentOffset.Base.z = 3.75 - 0.2
  expr: Constraints[16] = 15.5 - 0.4
  expr: Constraints[17] = -19.7 + 0.2
  expr: Constraints[18] = 11.4 - 0.4
  expr: Constraints[27] = 5 - 0.4
  sketch-geometry (10):
    g0: LineSegment StartX=5.5 StartY=-11.6 StartZ=0 EndX=5.5 EndY=-19.5 EndZ=0
    g1: LineSegment StartX=5.5 StartY=-19.5 StartZ=0 EndX=-5.5 EndY=-19.5 EndZ=0
    g2: LineSegment StartX=-5.5 StartY=-19.5 StartZ=0 EndX=-5.5 EndY=-11.6 EndZ=0
    g3: LineSegment StartX=-7.55 StartY=-7 StartZ=0 EndX=7.55 EndY=-7 EndZ=0
    g4: LineSegment StartX=7.55 StartY=-7 StartZ=0 EndX=7.55 EndY=-11.6 EndZ=0
    g5: LineSegment StartX=7.55 StartY=-11.6 StartZ=0 EndX=5.5 EndY=-11.6 EndZ=0
    g6: LineSegment StartX=-7.55 StartY=-11.6 StartZ=0 EndX=-7.55 EndY=-7 EndZ=0
    g7: LineSegment StartX=-5.5 StartY=-11.6 StartZ=0 EndX=-7.55 EndY=-11.6 EndZ=0
    g8: LineSegment StartX=5.5 StartY=-11.6 StartZ=0 EndX=5.5 EndY=-9.3 EndZ=0
    g9: LineSegment StartX=5.5 StartY=-9.3 StartZ=0 EndX=5.5 EndY=-7 EndZ=0
  constraints (28):
    c: Coincident(g0,g1)
    c: Coincident(g1,g2)
    c: Horizontal(g1)
    c: Vertical(g0)
    c: Vertical(g2)
    c: Coincident(g3,g4)
    c: Coincident(g4,g5)
    c: Coincident(g7,g6)
    c: Coincident(g6,g3)
    c: Horizontal(g5)
    c: Vertical(g4)
    c: Vertical(g6)
    c: Coincident(g5,g0)
    c: Coincident(g7,g2)
    c: Symmetric(g0,g2,g-2)
    c: Symmetric(g3,g3,g-2)
    c: DistanceX(g3,g3) = 15.1
    c: DistanceY(g0) = -19.5
    c: DistanceX(g2,g0) = 11
    c: Horizontal(g7)
    c: Coincident(g8,g0)
    c: Vertical(g8)
    c: Coincident(g9,g8)
    c: PointOnObject(g9,g3)
    c: Vertical(g9)
    c: Equal(g9,g8)
    c: DistanceY(g8) = -9.3
    c: DistanceY(g4,g4) = 4.6
FEATURE [PartDesign::CoordinateSystem] LCS_guts
  AttacherType = Attacher::AttachEngine3D
  MapMode = 45
  Placement = pos=(0,0,-9.3) rot=(0,0,1;1.5708rad)
  Support = -> [Mirrored009]
FEATURE [PartDesign::Body] Conn_Male002  label="Housing-USB_Male"
  Group = -> [LCS_002,Sketch013,Pad005,Sketch014,Pocket008,Sketch017,Pocket010,Sketch018,Pocket011,Chamfer002,Sketch019,Pocket012,Chamfer003,LCS_mag1,LCS_mag2,LCS_pin1,LCS_pin2,LCS_pin3,Sketch027,Pad009,Chamfer,LCS_bottom_edge,Sketch046,Pad021,LinearPattern001,Sketch047,Pad022,Mirrored008,Sketch048,Pad023,Mirrored009,Sketch049,LCS_guts]
  Origin = -> Origin008
  Tip = -> Mirrored009
COMPONENT P7 — recipe-attached ("Housing-USB-Male-Guts", modeled in this document).
Construction recipe (the document's own serialized feature program — sketch geometry with constraints, then the solid features built on it; lengths are millimeters unless a unit is written):

FEATURE [Sketcher::SketchObject] Sketch050
  AttachmentOffset = pos=(0,0,3.55) rot=(0,0,1;0rad)
  FullyConstrained = true
  MapMode = 5
  Placement = pos=(0,-3.55,8e-16) rot=(1,0,0;1.5708rad)
  Support = -> [XZ_Plane040]
  expr: .AttachmentOffset.Base.z = 3.75 - 0.2
  expr: Constraints[16] = 15.5 - 0.4
  expr: Constraints[17] = -19.7 + 0.2
  expr: Constraints[18] = 11.4 - 0.4
  expr: Constraints[27] = 5 - 0.4
  sketch-geometry (10):
    g0: LineSegment StartX=5.5 StartY=-11.6 StartZ=0 EndX=5.5 EndY=-19.5 EndZ=0
    g1: LineSegment StartX=5.5 StartY=-19.5 StartZ=0 EndX=-5.5 EndY=-19.5 EndZ=0
    g2: LineSegment StartX=-5.5 StartY=-19.5 StartZ=0 EndX=-5.5 EndY=-11.6 EndZ=0
    g3: LineSegment StartX=-7.55 StartY=-7 StartZ=0 EndX=7.55 EndY=-7 EndZ=0
    g4: LineSegment StartX=7.55 StartY=-7 StartZ=0 EndX=7.55 EndY=-11.6 EndZ=0
    g5: LineSegment StartX=7.55 StartY=-11.6 StartZ=0 EndX=5.5 EndY=-11.6 EndZ=0
    g6: LineSegment StartX=-7.55 StartY=-11.6 StartZ=0 EndX=-7.55 EndY=-7 EndZ=0
    g7: LineSegment StartX=-5.5 StartY=-11.6 StartZ=0 EndX=-7.55 EndY=-11.6 EndZ=0
    g8: LineSegment StartX=5.5 StartY=-11.6 StartZ=0 EndX=5.5 EndY=-9.3 EndZ=0
    g9: LineSegment StartX=5.5 StartY=-9.3 StartZ=0 EndX=5.5 EndY=-7 EndZ=0
  constraints (28):
    c: Coincident(g0,g1)
    c: Coincident(g1,g2)
    c: Horizontal(g1)
    c: Vertical(g0)
    c: Vertical(g2)
    c: Coincident(g3,g4)
    c: Coincident(g4,g5)
    c: Coincident(g7,g6)
    c: Coincident(g6,g3)
    c: Horizontal(g5)
    c: Vertical(g4)
    c: Vertical(g6)
    c: Coincident(g5,g0)
    c: Coincident(g7,g2)
    c: Symmetric(g0,g2,g-2)
    c: Symmetric(g3,g3,g-2)
    c: DistanceX(g3,g3) = 15.1
    c: DistanceY(g0) = -19.5
    c: DistanceX(g2,g0) = 11
    c: Horizontal(g7)
    c: Coincident(g8,g0)
    c: Vertical(g8)
    c: Coincident(g9,g8)
    c: PointOnObject(g9,g3)
    c: Vertical(g9)
    c: Equal(g9,g8)
    c: DistanceY(g8) = -9.3
    c: DistanceY(g4,g4) = 4.6
FEATURE [PartDesign::Pad] Pad024
  Direction = (0,-1,2e-16)
  Length = 7.1
  Length2 = 10
  Placement = pos=(0,0,0) rot=(1,0,0;1.5708rad)
  Profile = -> Sketch050
  ReferenceAxis = -> Sketch050 [N_Axis]
  Type = 0
  expr: Length = 7.5 - 0.4
FEATURE [PartDesign::CoordinateSystem] LCS_0  label="LCS_base001"
  AttacherType = Attacher::AttachEngine3D
  MapMode = 45
  Placement = pos=(0,-7.1,-9.3) rot=(0,0,1;1.5708rad)
  Support = -> [Pad024]
FEATURE [Sketcher::SketchObject] Sketch051
  FullyConstrained = true
  MapMode = 5
  Placement = pos=(0,0,0) rot=(0.57735,0.57735,0.57735;2.0944rad)
  Support = -> [YZ_Plane040]
  expr: Constraints[11] = -7 - 0.4
  expr: Constraints[9] = -19.7 + 0.2
  sketch-geometry (4):
    g0: LineSegment StartX=-7.4 StartY=-13 StartZ=0 EndX=0 EndY=-13 EndZ=0
    g1: LineSegment StartX=0 StartY=-13 StartZ=0 EndX=0 EndY=-19.5 EndZ=0
    g2: LineSegment StartX=0 StartY=-19.5 StartZ=0 EndX=-7.4 EndY=-19.5 EndZ=0
    g3: LineSegment StartX=-7.4 StartY=-19.5 StartZ=0 EndX=-7.4 EndY=-13 EndZ=0
  constraints (12):
    c: Coincident(g0,g1)
    c: Coincident(g1,g2)
    c: Coincident(g2,g3)
    c: Coincident(g3,g0)
    c: Horizontal(g0)
    c: Horizontal(g2)
    c: Vertical(g1)
    c: Vertical(g3)
    c: PointOnObject(g1,g-2)
    c: DistanceY(g2) = -19.5
    c: DistanceY(g3,g3) = 6.5
    c: DistanceX(g0) = -7.4
FEATURE [PartDesign::Pocket] Pocket035
  BaseFeature = -> Pad024
  Direction = (-1,2e-16,-3e-16)
  Length = 5
  Length2 = 5
  Midplane = true
  Placement = pos=(0,0,0) rot=(1,0,0;1.5708rad)
  Profile = -> Sketch051
  ReferenceAxis = -> Sketch051 [N_Axis]
  Type = 1
FEATURE [Sketcher::SketchObject] Sketch052
  FullyConstrained = true
  MapMode = 5
  Support = -> [XY_Plane040]
  sketch-geometry (4):
    g0: LineSegment StartX=-5 StartY=0 StartZ=0 EndX=5 EndY=0 EndZ=0
    g1: LineSegment StartX=5 StartY=0 StartZ=0 EndX=5 EndY=-7.5 EndZ=0
    g2: LineSegment StartX=5 StartY=-7.5 StartZ=0 EndX=-5 EndY=-7.5 EndZ=0
    g3: LineSegment StartX=-5 StartY=-7.5 StartZ=0 EndX=-5 EndY=0 EndZ=0
  constraints (11):
    c: Coincident(g0,g1)
    c: Coincident(g1,g2)
    c: Coincident(g2,g3)
    c: Coincident(g3,g0)
    c: Horizontal(g2)
    c: Vertical(g1)
    c: Vertical(g3)
    c: PointOnObject(g0,g-1)
    c: Symmetric(g0,g0,g-2)
    c: DistanceX(g0,g0) = 10
    c: DistanceY(g1,g1) = 7.5
FEATURE [PartDesign::Pocket] Pocket036
  BaseFeature = -> Pocket035
  Direction = (0,0,-1)
  Length = 5
  Length2 = 5
  Midplane = true
  Placement = pos=(0,0,0) rot=(1,0,0;1.5708rad)
  Profile = -> Sketch052
  ReferenceAxis = -> Sketch052 [N_Axis]
  Type = 1
FEATURE [Sketcher::SketchObject] Sketch053
  FullyConstrained = true
  MapMode = 5
  Support = -> [XY_Plane040]
  sketch-geometry (3):
    g0: Circle CenterX=0 CenterY=-8.6 CenterZ=0 NormalX=0 NormalY=0 NormalZ=1 AngleXU=0 Radius=0.75
    g1: Circle CenterX=2.9 CenterY=-8.6 CenterZ=0 NormalX=0 NormalY=0 NormalZ=1 AngleXU=0 Radius=0.75
    g2: Circle CenterX=-2.9 CenterY=-8.6 CenterZ=0 NormalX=0 NormalY=0 NormalZ=1 AngleXU=0 Radius=0.75
  constraints (8):
    c: PointOnObject(g0,g-2)
    c: Equal(g2,g0)
    c: Equal(g0,g1)
    c: Symmetric(g1,g2,g0)
    c: DistanceX(g0,g1) = 2.9
    c: Diameter(g1) = 1.5
    c: DistanceY(g0) = -8.6
    c: Horizontal(g1,g0)
FEATURE [PartDesign::Pocket] Pocket037
  BaseFeature = -> Pocket036
  Direction = (0,0,-1)
  Length = 32.5
  Length2 = 5
  Midplane = true
  Placement = pos=(0,0,0) rot=(1,0,0;1.5708rad)
  Profile = -> Sketch053
  ReferenceAxis = -> Sketch053 [N_Axis]
  Type = 0
FEATURE [PartDesign::Chamfer] Chamfer007
  Angle = 45
  Base = -> Pocket037 [Edge37,Edge36,Edge35]
  BaseFeature = -> Pocket037
  ChamferType = 0
  FlipDirection = false
  Placement = pos=(0,0,0) rot=(1,0,0;1.5708rad)
  Size = 0.25
  Size2 = 1
  SupportTransform = false
  UseAllEdges = false
FEATURE [PartDesign::Fillet] Fillet004
  Base = -> Chamfer007 [Edge3,Edge7,Edge19,Edge55,Edge51,Edge33]
  BaseFeature = -> Chamfer007
  Placement = pos=(0,0,0) rot=(1,0,0;1.5708rad)
  Radius = 0.4
  SupportTransform = false
  UseAllEdges = false
FEATURE [PartDesign::Chamfer] Chamfer008
  Angle = 45
  Base = -> Fillet004 [Edge4,Edge28,Edge14,Edge45]
  BaseFeature = -> Fillet004
  ChamferType = 0
  FlipDirection = false
  Placement = pos=(0,0,0) rot=(1,0,0;1.5708rad)
  Size = 0.25
  Size2 = 1
  SupportTransform = false
  UseAllEdges = false
FEATURE [PartDesign::Body] Housing_USB_Male_Guts  label="Housing-USB-Male-Guts"
  Group = -> [LCS_0,Sketch050,Pad024,Sketch051,Pocket035,Sketch052,Pocket036,Sketch053,Pocket037,Chamfer007,Fillet004,Chamfer008]
  Origin = -> Origin040
  Tip = -> Chamfer008
COMPONENT P8 — recipe-attached ("Magnet_Cube", modeled in this document).
Construction recipe (the document's own serialized feature program — sketch geometry with constraints, then the solid features built on it; lengths are millimeters unless a unit is written):

FEATURE [Sketcher::SketchObject] Sketch021
  FullyConstrained = true
  MapMode = 5
  Support = -> [XY_Plane019]
  sketch-geometry (4):
    g0: LineSegment StartX=-1.5 StartY=1.5 StartZ=0 EndX=1.5 EndY=1.5 EndZ=0
    g1: LineSegment StartX=1.5 StartY=1.5 StartZ=0 EndX=1.5 EndY=-1.5 EndZ=0
    g2: LineSegment StartX=1.5 StartY=-1.5 StartZ=0 EndX=-1.5 EndY=-1.5 EndZ=0
    g3: LineSegment StartX=-1.5 StartY=-1.5 StartZ=0 EndX=-1.5 EndY=1.5 EndZ=0
  constraints (11):
    c: Coincident(g0,g1)
    c: Coincident(g1,g2)
    c: Coincident(g2,g3)
    c: Coincident(g3,g0)
    c: Horizontal(g0)
    c: Horizontal(g2)
    c: Vertical(g1)
    c: Vertical(g3)
    c: Symmetric(g1,g0,g-1)
    c: Equal(g1,g0)
    c: DistanceX(g0,g0) = 3
FEATURE [PartDesign::Pad] Pad006
  Direction = (0,0,1)
  Length = 3
  Length2 = 10
  Profile = -> Sketch021
  ReferenceAxis = -> Sketch021 [N_Axis]
  Type = 0
FEATURE [PartDesign::Fillet] Fillet002
  Base = -> Pad006 [Edge9,Edge8,Edge11,Edge6,Edge3,Edge2,Edge1,Edge5,Edge7,Edge12,Edge10,Edge4]
  BaseFeature = -> Pad006
  Radius = 0.1
  SupportTransform = false
  UseAllEdges = false
FEATURE [PartDesign::CoordinateSystem] LCS_004
  AttacherType = Attacher::AttachEngine3D
  MapMode = 45
  Placement = pos=(0,1e-16,0) rot=(0,0,1;0rad)
  Support = -> [Fillet002]
FEATURE [PartDesign::Body] Magnet  label="Magnet_Cube"
  Group = -> [LCS_004,Sketch021,Pad006,Fillet002]
  Origin = -> Origin019
  Tip = -> Fillet002
COMPONENT P9 — geometry summary ("Conn_USB_Male"; no construction recipe available for this part):
  bounding box: 21.0 x 12.0 x 4.5 mm
  tessellated surface: 2,060 triangles
  volume: 699 mm^3 (62% of its bounding box)
  symmetry: mirror-symmetric across its x mid-plane
COMPONENT P10 — recipe-attached ("Conn_USB_Female", modeled in this document).
Construction recipe (the document's own serialized feature program — sketch geometry with constraints, then the solid features built on it; lengths are millimeters unless a unit is written):

FEATURE [PartDesign::FeatureBase] Clone007
  BaseFeature = -> Part__Feature
FEATURE [Sketcher::SketchObject] Sketch039
  FullyConstrained = false
  MapMode = 5
  Placement = pos=(0,0,0) rot=(1,0,0;1.5708rad)
  Support = -> [XZ_Plane037]
  sketch-geometry (4):
    g0: LineSegment StartX=9.5 StartY=-19.5588 StartZ=0 EndX=5.5 EndY=-19.5588 EndZ=0
    g1: LineSegment StartX=5.5 StartY=-19.5588 StartZ=0 EndX=5.5 EndY=-15 EndZ=0
    g2: LineSegment StartX=5.5 StartY=-15 StartZ=0 EndX=9.5 EndY=-15 EndZ=0
    g3: LineSegment StartX=9.5 StartY=-15 StartZ=0 EndX=9.5 EndY=-19.5588 EndZ=0
  constraints (11):
    c: Coincident(g0,g1)
    c: Coincident(g1,g2)
    c: Coincident(g2,g3)
    c: Coincident(g3,g0)
    c: Horizontal(g0)
    c: Horizontal(g2)
    c: Vertical(g1)
    c: Vertical(g3)
    c: DistanceY(g1) = -15
    c: DistanceX(g0,g0) = 4
    c: DistanceX(g1) = 5.5
FEATURE [PartDesign::Pocket] Pocket028
  BaseFeature = -> Clone007
  Direction = (0,1,-2e-16)
  Length = 5
  Length2 = 5
  Midplane = true
  Profile = -> Sketch039
  ReferenceAxis = -> Sketch039 [N_Axis]
  Type = 1
FEATURE [PartDesign::Mirrored] Mirrored006
  BaseFeature = -> Pocket028
  MirrorPlane = -> Sketch039 [V_Axis]
  Originals = -> [Pocket028]
FEATURE [Sketcher::SketchObject] Sketch040
  AttachmentOffset = pos=(0,0,6.55) rot=(0,0,1;0rad)
  FullyConstrained = true
  MapMode = 5
  Placement = pos=(6.55,-1.5e-15,1.5e-15) rot=(0.57735,0.57735,0.57735;2.0944rad)
  Support = -> [YZ_Plane037]
  sketch-geometry (6):
    g0: LineSegment StartX=2.5 StartY=-15 StartZ=0 EndX=2.65 EndY=-17.6441 EndZ=0
    g1: LineSegment StartX=4.25 StartY=-17.6441 StartZ=0 EndX=4.4 EndY=-15 EndZ=0
    g2: ArcOfCircle CenterX=3.45 CenterY=-17.5987 CenterZ=0 NormalX=0 NormalY=0 NormalZ=1 AngleXU=0 Radius=0.801286 StartAngle=3.19826 EndAngle=6.22652
    g3: LineSegment StartX=2.5 StartY=-15 StartZ=0 EndX=3.45 EndY=-15 EndZ=0
    g4: LineSegment StartX=3.45 StartY=-15 StartZ=0 EndX=4.4 EndY=-15 EndZ=0
    g5: GeomPoint X=3.45 Y=-18.4 Z=0
  constraints (16):
    c: Tangent(g2,g1) = -1.5708
    c: Tangent(g2,g0) = -1.5708
    c: Coincident(g3,g0)
    c: Horizontal(g3)
    c: Coincident(g4,g3)
    c: Coincident(g4,g1)
    c: Horizontal(g4)
    c: Equal(g4,g3)
    c: DistanceX(g3) = 3.45
    c: DistanceY(g1) = -15
    c: PointOnObject(g5,g2)
    c: Vertical(g5,g2)
    c: DistanceY(g5,g1) = 3.4
    c: DistanceX(g0,g1) = 1.9
    c: Equal(g1,g0)
    c: DistanceX(g0,g1) = 1.6
FEATURE [PartDesign::Pad] Pad015  label="tab"
  BaseFeature = -> Mirrored006
  Direction = (1,-2e-16,3e-16)
  Length = 0.3
  Length2 = 10
  Profile = -> Sketch040
  ReferenceAxis = -> Sketch040 [N_Axis]
  Reversed = true
  Type = 0
FEATURE [PartDesign::Mirrored] Mirrored007
  BaseFeature = -> Pad015
  MirrorPlane = -> YZ_Plane037
  Originals = -> [Pad015]
FEATURE [Sketcher::SketchObject] Sketch041
  FullyConstrained = true
  MapMode = 5
  Placement = pos=(0,0,0) rot=(1,0,0;1.5708rad)
  Support = -> [XZ_Plane037]
  expr: Constraints[7] = -15 - 2.3
  sketch-geometry (4):
    g0: LineSegment StartX=-5 StartY=-17.3 StartZ=0 EndX=5 EndY=-17.3 EndZ=0
    g1: LineSegment StartX=5 StartY=-17.3 StartZ=0 EndX=5 EndY=-18.3 EndZ=0
    g2: LineSegment StartX=5 StartY=-18.3 StartZ=0 EndX=-5 EndY=-18.3 EndZ=0
    g3: LineSegment StartX=-5 StartY=-18.3 StartZ=0 EndX=-5 EndY=-17.3 EndZ=0
  constraints (11):
    c: Coincident(g0,g1)
    c: Coincident(g1,g2)
    c: Coincident(g2,g3)
    c: Coincident(g3,g0)
    c: Horizontal(g2)
    c: Vertical(g1)
    c: Vertical(g3)
    c: DistanceY(g0) = -17.3
    c: Symmetric(g0,g0,g-2)
    c: DistanceX(g2,g2) = 10
    c: DistanceY(g1,g1) = 1
FEATURE [PartDesign::Pocket] Pocket029
  BaseFeature = -> Mirrored007
  Direction = (0,1,-2e-16)
  Length = 5
  Length2 = 5
  Profile = -> Sketch041
  ReferenceAxis = -> Sketch041 [N_Axis]
  Type = 1
FEATURE [PartDesign::Body] Body008  label="usb3_mod"
  BaseFeature = -> Part__Feature
  Group = -> [Clone007,Sketch039,Pocket028,Mirrored006,Sketch040,Pad015,Mirrored007,Sketch041,Pocket029]
  Origin = -> Origin037
  Tip = -> Pocket029
COMPONENT P11 — geometry summary ("Pogo-Pin_Set"; no construction recipe available for this part):
  bounding box: 16.8 x 1.0 x 1.0 mm
  tessellated surface: 8,500 triangles
  volume: 18 mm^3 (96% of its bounding box)
  symmetry: 2-fold rotationally symmetric about the x axis; mirror-symmetric across its y mid-plane, z mid-plane
COMPONENT P12 — recipe-attached ("Pogo-Contact", modeled in this document).
Construction recipe (the document's own serialized feature program — sketch geometry with constraints, then the solid features built on it; lengths are millimeters unless a unit is written):

FEATURE [Sketcher::SketchObject] Sketch035
  FullyConstrained = true
  MapMode = 5
  Support = -> [XY_Plane036]
  expr: Constraints[10] = 2 * 3.25
  sketch-geometry (4):
    g0: LineSegment StartX=-3.25 StartY=0.95 StartZ=0 EndX=3.25 EndY=0.95 EndZ=0
    g1: LineSegment StartX=3.25 StartY=0.95 StartZ=0 EndX=3.25 EndY=-0.95 EndZ=0
    g2: LineSegment StartX=3.25 StartY=-0.95 StartZ=0 EndX=-3.25 EndY=-0.95 EndZ=0
    g3: LineSegment StartX=-3.25 StartY=-0.95 StartZ=0 EndX=-3.25 EndY=0.95 EndZ=0
  constraints (11):
    c: Coincident(g0,g1)
    c: Coincident(g1,g2)
    c: Coincident(g2,g3)
    c: Coincident(g3,g0)
    c: Horizontal(g0)
    c: Horizontal(g2)
    c: Vertical(g1)
    c: Vertical(g3)
    c: Symmetric(g0,g1,g-1)
    c: DistanceY(g1,g1) = 1.9
    c: DistanceX(g0,g0) = 6.5
FEATURE [PartDesign::Pad] Pad012
  Direction = (0,0,1)
  Length = 0.2
  Length2 = 10
  Profile = -> Sketch035
  ReferenceAxis = -> Sketch035 [N_Axis]
  Type = 0
FEATURE [PartDesign::FeaturePython] Bend  # WARN: FeaturePython — macro-defined, semantics opaque (R4)
  AutoMiter = true
  BaseFeature = -> Pad012
  BendType = 0
  LengthList = [4]
  LengthSpec = 0
  ReliefFactor = 0.7
  UseReliefFactor = false
  angle = 90
  baseObject = -> Pad012 [Face2]
  bendAList = [90]
  extend1 = 0
  extend2 = 0
  gap1 = 0
  gap2 = 0
  invert = false
  kfactor = 0.5
  length = 4
  maxExtendDist = 4
  minGap = 0.1
  minReliefGap = 1
  miterangle1 = 0
  miterangle2 = 0
  offset = 0
  radius = 0.01
  reliefType = 0
  reliefd = 1
  reliefw = 0.8
  sketchflip = false
  sketchinvert = false
  unfold = false
FEATURE [PartDesign::FeaturePython] Bend001  # WARN: FeaturePython — macro-defined, semantics opaque (R4)
  AutoMiter = true
  BaseFeature = -> Bend
  BendType = 0
  LengthList = [3]
  LengthSpec = 0
  ReliefFactor = 0.7
  UseReliefFactor = false
  angle = 90
  baseObject = -> Bend [Face3]
  bendAList = [90]
  extend1 = 0
  extend2 = 0
  gap1 = 0
  gap2 = 0
  invert = false
  kfactor = 0.5
  length = 3
  maxExtendDist = 5
  minGap = 0.1
  minReliefGap = 1
  miterangle1 = 0
  miterangle2 = 0
  offset = 0
  radius = 0.01
  reliefType = 0
  reliefd = 1
  reliefw = 0.8
  sketchflip = false
  sketchinvert = false
  unfold = false
FEATURE [PartDesign::FeaturePython] Bend002  # WARN: FeaturePython — macro-defined, semantics opaque (R4)
  AutoMiter = true
  BaseFeature = -> Bend001
  BendType = 0
  LengthList = [4]
  LengthSpec = 0
  ReliefFactor = 0.7
  UseReliefFactor = false
  angle = 90
  baseObject = -> Bend001 [Face21]
  bendAList = [90]
  extend1 = 0
  extend2 = 0
  gap1 = 0
  gap2 = 0
  invert = false
  kfactor = 0.5
  length = 4
  maxExtendDist = 5
  minGap = 0.1
  minReliefGap = 1
  miterangle1 = 0
  miterangle2 = 0
  offset = 0
  radius = 0.01
  reliefType = 0
  reliefd = 1
  reliefw = 0.8
  sketchflip = false
  sketchinvert = false
  unfold = false
FEATURE [PartDesign::FeaturePython] Bend003  # WARN: FeaturePython — macro-defined, semantics opaque (R4)
  AutoMiter = true
  BaseFeature = -> Bend002
  BendType = 0
  LengthList = [3.5]
  LengthSpec = 0
  ReliefFactor = 0.7
  UseReliefFactor = false
  angle = 90
  baseObject = -> Bend002 [Face3]
  bendAList = [90]
  extend1 = 0
  extend2 = 0
  gap1 = 0
  gap2 = 0
  invert = false
  kfactor = 0.5
  length = 3.5
  maxExtendDist = 5
  minGap = 0.1
  minReliefGap = 1
  miterangle1 = 0
  miterangle2 = 0
  offset = 0
  radius = 0.01
  reliefType = 0
  reliefd = 1
  reliefw = 0.8
  sketchflip = false
  sketchinvert = false
  unfold = false
FEATURE [PartDesign::CoordinateSystem] LCS_010  label="LCS_base"
  AttacherType = Attacher::AttachEngine3D
  MapMode = 45
  Placement = pos=(0,0,0.2) rot=(0,0,1;1.5708rad)
  Support = -> [Bend003]
FEATURE [PartDesign::Body] Pogo_Contact002  label="Pogo-Contact"
  Group = -> [LCS_010,Sketch035,Pad012,Bend,Bend001,Bend002,Bend003]
  Origin = -> Origin036
  Placement = pos=(0,0,0) rot=(0.57735,0.57735,0.57735;2.0944rad)
  Tip = -> Bend003
PROVENANCE & LICENSES
A FreeCAD (.FCStd) document from a public repository crawl; recipes are the document's own serialized feature recipes (and, for linked parts, companion documents' recipes).
License: gpl-3.0.
